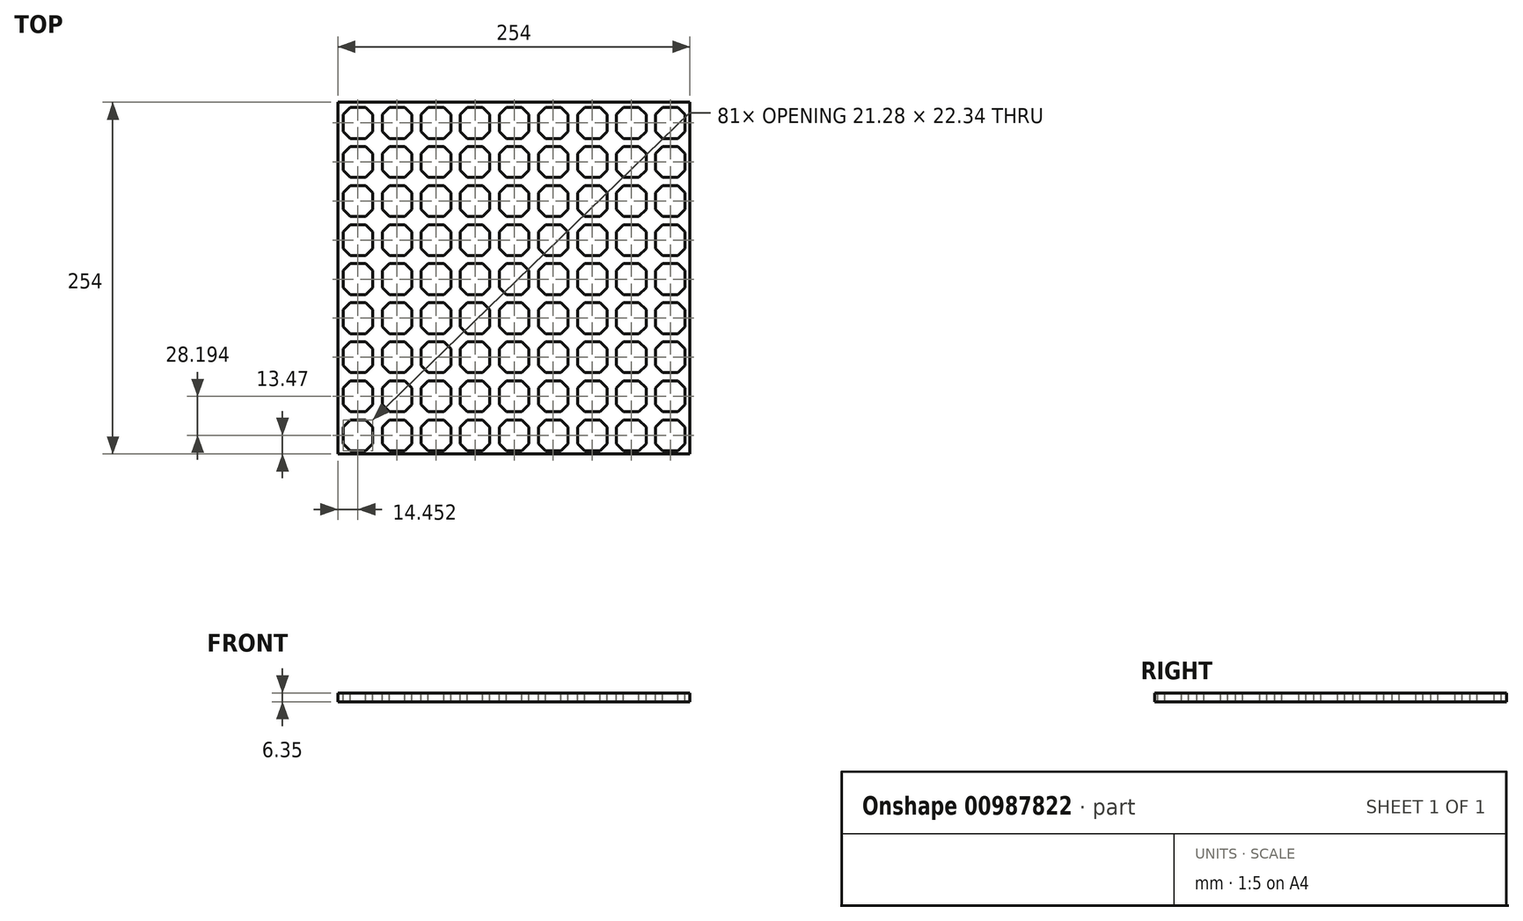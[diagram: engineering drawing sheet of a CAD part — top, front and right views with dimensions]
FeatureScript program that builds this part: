
annotation { "Feature Type Name" : "Feature", "Feature Type Description" : "" }
export const myFeature = defineFeature(function(context is Context, id is Id, definition is map)
    precondition{}
    {
        {
            var Q0;
            Q0=qCreatedBy(makeId("Top.planeOp"),FACE);
            var sketch = newSketch(context, id + "F0", { "sketchPlane" : qUnion([Q0])});
            skLineSegment(sketch, "E0.bottom", {"start": v(-127, 127) * mm, "end": v(127, 127) * mm});
            skLineSegment(sketch, "E0.top", {"start": v(-127, -127) * mm, "end": v(127, -127) * mm});
            skLineSegment(sketch, "E0.left", {"start": v(-127, 127) * mm, "end": v(-127, -127) * mm});
            skLineSegment(sketch, "E0.right", {"start": v(127, 127) * mm, "end": v(127, -127) * mm});
            skSolve(sketch);
        }
        {
            var Q0;
            Q0=qSketchRegion(id+"F0",true);
            extrude(context, id + "F1", {"entities" : qUnion([Q0]), "depth" : 6.35 * mm, "offsetDistance" : 25.4 * mm});
        }
        {
            var Q0;
            Q0=makeQuery(id+"F1.opExtrude","CAP_FACE",FACE,{"disambiguationData":[OSD([sQuery(id+"F0.wireOp",EDGE,"E0.bottom"),sQuery(id+"F0.wireOp",EDGE,"E0.top"),sQuery(id+"F0.wireOp",EDGE,"E0.left"),sQuery(id+"F0.wireOp",EDGE,"E0.right")])],"isStart":false});
            var sketch = newSketch(context, id + "F2", { "sketchPlane" : qUnion([Q0])});
            skLineSegment(sketch, "E1.bottom", {"start": v(-118.11, 123.2) * mm, "end": v(-106.99, 123.2) * mm});
            skLineSegment(sketch, "E1.top", {"start": v(-118.11, 100.85) * mm, "end": v(-106.99, 100.85) * mm});
            skLineSegment(sketch, "E1.left", {"start": v(-123.2, 118.11) * mm, "end": v(-123.2, 105.93) * mm});
            skLineSegment(sketch, "E1.right", {"start": v(-101.9, 118.11) * mm, "end": v(-101.9, 105.93) * mm});
            skLineSegment(sketch, "E2", {"start": v(-123.2, 118.11) * mm, "end": v(-118.11, 123.2) * mm});
            skPoint(sketch, "E3.orphan", {"position": v(-123.2, 123.2) * mm});
            skLineSegment(sketch, "E4", {"start": v(-106.99, 123.2) * mm, "end": v(-101.9, 118.11) * mm});
            skLineSegment(sketch, "E5", {"start": v(-123.2, 105.93) * mm, "end": v(-118.11, 100.85) * mm});
            skLineSegment(sketch, "E6", {"start": v(-101.9, 105.93) * mm, "end": v(-106.99, 100.85) * mm});
            skPoint(sketch, "E7.orphan", {"position": v(-101.9, 123.2) * mm});
            skPoint(sketch, "E8.orphan", {"position": v(-101.9, 100.85) * mm});
            skPoint(sketch, "E9.orphan", {"position": v(-123.2, 100.85) * mm});
            skLineSegment(sketch, "E10.1.0.0", {"start": v(-73.71, 118.11) * mm, "end": v(-73.71, 105.93) * mm});
            skLineSegment(sketch, "E10.1.0.1", {"start": v(-95, 118.11) * mm, "end": v(-95, 105.93) * mm});
            skLineSegment(sketch, "E10.1.0.2", {"start": v(-89.92, 100.85) * mm, "end": v(-78.8, 100.85) * mm});
            skLineSegment(sketch, "E10.1.0.3", {"start": v(-89.92, 123.2) * mm, "end": v(-78.8, 123.2) * mm});
            skPoint(sketch, "E10.1.0.4", {"position": v(-95, 123.2) * mm});
            skPoint(sketch, "E10.1.0.5", {"position": v(-73.71, 100.85) * mm});
            skPoint(sketch, "E10.1.0.6", {"position": v(-73.71, 123.2) * mm});
            skPoint(sketch, "E10.1.0.7", {"position": v(-95, 100.85) * mm});
            skLineSegment(sketch, "E10.1.0.8", {"start": v(-95, 118.11) * mm, "end": v(-89.92, 123.2) * mm});
            skLineSegment(sketch, "E10.1.0.9", {"start": v(-95, 105.93) * mm, "end": v(-89.92, 100.85) * mm});
            skLineSegment(sketch, "E10.1.0.10", {"start": v(-78.8, 123.2) * mm, "end": v(-73.71, 118.11) * mm});
            skLineSegment(sketch, "E10.1.0.11", {"start": v(-73.71, 105.93) * mm, "end": v(-78.8, 100.85) * mm});
            skLineSegment(sketch, "E10.2.0.0", {"start": v(-45.52, 118.11) * mm, "end": v(-45.52, 105.93) * mm});
            skLineSegment(sketch, "E10.2.0.1", {"start": v(-66.8, 118.11) * mm, "end": v(-66.8, 105.93) * mm});
            skLineSegment(sketch, "E10.2.0.2", {"start": v(-61.72, 100.85) * mm, "end": v(-50.6, 100.85) * mm});
            skLineSegment(sketch, "E10.2.0.3", {"start": v(-61.72, 123.2) * mm, "end": v(-50.6, 123.2) * mm});
            skPoint(sketch, "E10.2.0.4", {"position": v(-66.8, 123.2) * mm});
            skPoint(sketch, "E10.2.0.5", {"position": v(-45.52, 100.85) * mm});
            skPoint(sketch, "E10.2.0.6", {"position": v(-45.52, 123.2) * mm});
            skPoint(sketch, "E10.2.0.7", {"position": v(-66.8, 100.85) * mm});
            skLineSegment(sketch, "E10.2.0.8", {"start": v(-66.8, 118.11) * mm, "end": v(-61.72, 123.2) * mm});
            skLineSegment(sketch, "E10.2.0.9", {"start": v(-66.8, 105.93) * mm, "end": v(-61.72, 100.85) * mm});
            skLineSegment(sketch, "E10.2.0.10", {"start": v(-50.6, 123.2) * mm, "end": v(-45.52, 118.11) * mm});
            skLineSegment(sketch, "E10.2.0.11", {"start": v(-45.52, 105.93) * mm, "end": v(-50.6, 100.85) * mm});
            skLineSegment(sketch, "E10.3.0.0", {"start": v(-17.32, 118.11) * mm, "end": v(-17.32, 105.93) * mm});
            skLineSegment(sketch, "E10.3.0.1", {"start": v(-38.6, 118.11) * mm, "end": v(-38.6, 105.93) * mm});
            skLineSegment(sketch, "E10.3.0.2", {"start": v(-33.53, 100.85) * mm, "end": v(-22.4, 100.85) * mm});
            skLineSegment(sketch, "E10.3.0.3", {"start": v(-33.53, 123.2) * mm, "end": v(-22.4, 123.2) * mm});
            skPoint(sketch, "E10.3.0.4", {"position": v(-38.6, 123.2) * mm});
            skPoint(sketch, "E10.3.0.5", {"position": v(-17.32, 100.85) * mm});
            skPoint(sketch, "E10.3.0.6", {"position": v(-17.32, 123.2) * mm});
            skPoint(sketch, "E10.3.0.7", {"position": v(-38.6, 100.85) * mm});
            skLineSegment(sketch, "E10.3.0.8", {"start": v(-38.6, 118.11) * mm, "end": v(-33.53, 123.2) * mm});
            skLineSegment(sketch, "E10.3.0.9", {"start": v(-38.6, 105.93) * mm, "end": v(-33.53, 100.85) * mm});
            skLineSegment(sketch, "E10.3.0.10", {"start": v(-22.4, 123.2) * mm, "end": v(-17.32, 118.11) * mm});
            skLineSegment(sketch, "E10.3.0.11", {"start": v(-17.32, 105.93) * mm, "end": v(-22.4, 100.85) * mm});
            skLineSegment(sketch, "E10.4.0.0", {"start": v(10.87, 118.11) * mm, "end": v(10.87, 105.93) * mm});
            skLineSegment(sketch, "E10.4.0.1", {"start": v(-10.41, 118.11) * mm, "end": v(-10.41, 105.93) * mm});
            skLineSegment(sketch, "E10.4.0.2", {"start": v(-5.33, 100.85) * mm, "end": v(5.79, 100.85) * mm});
            skLineSegment(sketch, "E10.4.0.3", {"start": v(-5.33, 123.2) * mm, "end": v(5.79, 123.2) * mm});
            skPoint(sketch, "E10.4.0.4", {"position": v(-10.41, 123.2) * mm});
            skPoint(sketch, "E10.4.0.5", {"position": v(10.87, 100.85) * mm});
            skPoint(sketch, "E10.4.0.6", {"position": v(10.87, 123.2) * mm});
            skPoint(sketch, "E10.4.0.7", {"position": v(-10.41, 100.85) * mm});
            skLineSegment(sketch, "E10.4.0.8", {"start": v(-10.41, 118.11) * mm, "end": v(-5.33, 123.2) * mm});
            skLineSegment(sketch, "E10.4.0.9", {"start": v(-10.41, 105.93) * mm, "end": v(-5.33, 100.85) * mm});
            skLineSegment(sketch, "E10.4.0.10", {"start": v(5.79, 123.2) * mm, "end": v(10.87, 118.11) * mm});
            skLineSegment(sketch, "E10.4.0.11", {"start": v(10.87, 105.93) * mm, "end": v(5.79, 100.85) * mm});
            skLineSegment(sketch, "E10.5.0.0", {"start": v(39.06, 118.11) * mm, "end": v(39.06, 105.93) * mm});
            skLineSegment(sketch, "E10.5.0.1", {"start": v(17.78, 118.11) * mm, "end": v(17.78, 105.93) * mm});
            skLineSegment(sketch, "E10.5.0.2", {"start": v(22.86, 100.85) * mm, "end": v(33.98, 100.85) * mm});
            skLineSegment(sketch, "E10.5.0.3", {"start": v(22.86, 123.2) * mm, "end": v(33.98, 123.2) * mm});
            skPoint(sketch, "E10.5.0.4", {"position": v(17.78, 123.2) * mm});
            skPoint(sketch, "E10.5.0.5", {"position": v(39.06, 100.85) * mm});
            skPoint(sketch, "E10.5.0.6", {"position": v(39.06, 123.2) * mm});
            skPoint(sketch, "E10.5.0.7", {"position": v(17.78, 100.85) * mm});
            skLineSegment(sketch, "E10.5.0.8", {"start": v(17.78, 118.11) * mm, "end": v(22.86, 123.2) * mm});
            skLineSegment(sketch, "E10.5.0.9", {"start": v(17.78, 105.93) * mm, "end": v(22.86, 100.85) * mm});
            skLineSegment(sketch, "E10.5.0.10", {"start": v(33.98, 123.2) * mm, "end": v(39.06, 118.11) * mm});
            skLineSegment(sketch, "E10.5.0.11", {"start": v(39.06, 105.93) * mm, "end": v(33.98, 100.85) * mm});
            skLineSegment(sketch, "E10.6.0.0", {"start": v(67.26, 118.11) * mm, "end": v(67.26, 105.93) * mm});
            skLineSegment(sketch, "E10.6.0.1", {"start": v(45.97, 118.11) * mm, "end": v(45.97, 105.93) * mm});
            skLineSegment(sketch, "E10.6.0.2", {"start": v(51.05, 100.85) * mm, "end": v(62.18, 100.85) * mm});
            skLineSegment(sketch, "E10.6.0.3", {"start": v(51.05, 123.2) * mm, "end": v(62.18, 123.2) * mm});
            skPoint(sketch, "E10.6.0.4", {"position": v(45.97, 123.2) * mm});
            skPoint(sketch, "E10.6.0.5", {"position": v(67.26, 100.85) * mm});
            skPoint(sketch, "E10.6.0.6", {"position": v(67.26, 123.2) * mm});
            skPoint(sketch, "E10.6.0.7", {"position": v(45.97, 100.85) * mm});
            skLineSegment(sketch, "E10.6.0.8", {"start": v(45.97, 118.11) * mm, "end": v(51.05, 123.2) * mm});
            skLineSegment(sketch, "E10.6.0.9", {"start": v(45.97, 105.93) * mm, "end": v(51.05, 100.85) * mm});
            skLineSegment(sketch, "E10.6.0.10", {"start": v(62.18, 123.2) * mm, "end": v(67.26, 118.11) * mm});
            skLineSegment(sketch, "E10.6.0.11", {"start": v(67.26, 105.93) * mm, "end": v(62.18, 100.85) * mm});
            skLineSegment(sketch, "E10.7.0.0", {"start": v(95.45, 118.11) * mm, "end": v(95.45, 105.93) * mm});
            skLineSegment(sketch, "E10.7.0.1", {"start": v(74.17, 118.11) * mm, "end": v(74.17, 105.93) * mm});
            skLineSegment(sketch, "E10.7.0.2", {"start": v(79.25, 100.85) * mm, "end": v(90.37, 100.85) * mm});
            skLineSegment(sketch, "E10.7.0.3", {"start": v(79.25, 123.2) * mm, "end": v(90.37, 123.2) * mm});
            skPoint(sketch, "E10.7.0.4", {"position": v(74.17, 123.2) * mm});
            skPoint(sketch, "E10.7.0.5", {"position": v(95.45, 100.85) * mm});
            skPoint(sketch, "E10.7.0.6", {"position": v(95.45, 123.2) * mm});
            skPoint(sketch, "E10.7.0.7", {"position": v(74.17, 100.85) * mm});
            skLineSegment(sketch, "E10.7.0.8", {"start": v(74.17, 118.11) * mm, "end": v(79.25, 123.2) * mm});
            skLineSegment(sketch, "E10.7.0.9", {"start": v(74.17, 105.93) * mm, "end": v(79.25, 100.85) * mm});
            skLineSegment(sketch, "E10.7.0.10", {"start": v(90.37, 123.2) * mm, "end": v(95.45, 118.11) * mm});
            skLineSegment(sketch, "E10.7.0.11", {"start": v(95.45, 105.93) * mm, "end": v(90.37, 100.85) * mm});
            skLineSegment(sketch, "E10.8.0.0", {"start": v(123.65, 118.11) * mm, "end": v(123.65, 105.93) * mm});
            skLineSegment(sketch, "E10.8.0.1", {"start": v(102.36, 118.11) * mm, "end": v(102.36, 105.93) * mm});
            skLineSegment(sketch, "E10.8.0.2", {"start": v(107.44, 100.85) * mm, "end": v(118.57, 100.85) * mm});
            skLineSegment(sketch, "E10.8.0.3", {"start": v(107.44, 123.2) * mm, "end": v(118.57, 123.2) * mm});
            skPoint(sketch, "E10.8.0.4", {"position": v(102.36, 123.2) * mm});
            skPoint(sketch, "E10.8.0.5", {"position": v(123.65, 100.85) * mm});
            skPoint(sketch, "E10.8.0.6", {"position": v(123.65, 123.2) * mm});
            skPoint(sketch, "E10.8.0.7", {"position": v(102.36, 100.85) * mm});
            skLineSegment(sketch, "E10.8.0.8", {"start": v(102.36, 118.11) * mm, "end": v(107.44, 123.2) * mm});
            skLineSegment(sketch, "E10.8.0.9", {"start": v(102.36, 105.93) * mm, "end": v(107.44, 100.85) * mm});
            skLineSegment(sketch, "E10.8.0.10", {"start": v(118.57, 123.2) * mm, "end": v(123.65, 118.11) * mm});
            skLineSegment(sketch, "E10.8.0.11", {"start": v(123.65, 105.93) * mm, "end": v(118.57, 100.85) * mm});
            skLineSegment(sketch, "E10.9.0.0", {"start": v(151.84, 118.11) * mm, "end": v(151.84, 105.93) * mm});
            skLineSegment(sketch, "E10.9.0.1", {"start": v(130.56, 118.11) * mm, "end": v(130.56, 105.93) * mm});
            skLineSegment(sketch, "E10.9.0.2", {"start": v(135.64, 100.85) * mm, "end": v(146.76, 100.85) * mm});
            skLineSegment(sketch, "E10.9.0.3", {"start": v(135.64, 123.2) * mm, "end": v(146.76, 123.2) * mm});
            skPoint(sketch, "E10.9.0.4", {"position": v(130.56, 123.2) * mm});
            skPoint(sketch, "E10.9.0.5", {"position": v(151.84, 100.85) * mm});
            skPoint(sketch, "E10.9.0.6", {"position": v(151.84, 123.2) * mm});
            skPoint(sketch, "E10.9.0.7", {"position": v(130.56, 100.85) * mm});
            skLineSegment(sketch, "E10.9.0.8", {"start": v(130.56, 118.11) * mm, "end": v(135.64, 123.2) * mm});
            skLineSegment(sketch, "E10.9.0.9", {"start": v(130.56, 105.93) * mm, "end": v(135.64, 100.85) * mm});
            skLineSegment(sketch, "E10.9.0.10", {"start": v(146.76, 123.2) * mm, "end": v(151.84, 118.11) * mm});
            skLineSegment(sketch, "E10.9.0.11", {"start": v(151.84, 105.93) * mm, "end": v(146.76, 100.85) * mm});
            skLineSegment(sketch, "E10.direction1", {"start": v(-123.2, 100.85) * mm, "end": v(-95, 100.85) * mm, "construction": true});
            skPoint(sketch, "E11.0.1.0", {"position": v(-73.71, 95) * mm});
            skLineSegment(sketch, "E11.0.1.1", {"start": v(102.36, 89.92) * mm, "end": v(102.36, 77.74) * mm});
            skLineSegment(sketch, "E11.0.1.2", {"start": v(45.97, 89.92) * mm, "end": v(45.97, 77.74) * mm});
            skPoint(sketch, "E11.0.1.3", {"position": v(39.06, 95) * mm});
            skLineSegment(sketch, "E11.0.1.4", {"start": v(-66.8, 89.92) * mm, "end": v(-66.8, 77.74) * mm});
            skLineSegment(sketch, "E11.0.1.5", {"start": v(-95, 89.92) * mm, "end": v(-95, 77.74) * mm});
            skLineSegment(sketch, "E11.0.1.6", {"start": v(-73.71, 89.92) * mm, "end": v(-73.71, 77.74) * mm});
            skLineSegment(sketch, "E11.0.1.7", {"start": v(-123.2, 89.92) * mm, "end": v(-123.2, 77.74) * mm});
            skLineSegment(sketch, "E11.0.1.8", {"start": v(-101.9, 89.92) * mm, "end": v(-101.9, 77.74) * mm});
            skPoint(sketch, "E11.0.1.9", {"position": v(130.56, 72.66) * mm});
            skPoint(sketch, "E11.0.1.10", {"position": v(67.26, 95) * mm});
            skPoint(sketch, "E11.0.1.11", {"position": v(-66.8, 72.66) * mm});
            skPoint(sketch, "E11.0.1.12", {"position": v(10.87, 95) * mm});
            skPoint(sketch, "E11.0.1.13", {"position": v(-101.9, 72.66) * mm});
            skPoint(sketch, "E11.0.1.14", {"position": v(45.97, 72.66) * mm});
            skLineSegment(sketch, "E11.0.1.15", {"start": v(-118.11, 95) * mm, "end": v(-106.99, 95) * mm});
            skPoint(sketch, "E11.0.1.16", {"position": v(-45.52, 95) * mm});
            skPoint(sketch, "E11.0.1.17", {"position": v(151.84, 95) * mm});
            skPoint(sketch, "E11.0.1.18", {"position": v(123.65, 95) * mm});
            skLineSegment(sketch, "E11.0.1.19", {"start": v(151.84, 89.92) * mm, "end": v(151.84, 77.74) * mm});
            skLineSegment(sketch, "E11.0.1.20", {"start": v(95.45, 89.92) * mm, "end": v(95.45, 77.74) * mm});
            skLineSegment(sketch, "E11.0.1.21", {"start": v(39.06, 89.92) * mm, "end": v(39.06, 77.74) * mm});
            skLineSegment(sketch, "E11.0.1.22", {"start": v(-17.32, 89.92) * mm, "end": v(-17.32, 77.74) * mm});
            skPoint(sketch, "E11.0.1.23", {"position": v(74.17, 72.66) * mm});
            skPoint(sketch, "E11.0.1.24", {"position": v(-38.6, 72.66) * mm});
            skLineSegment(sketch, "E11.0.1.25", {"start": v(-10.41, 89.92) * mm, "end": v(-10.41, 77.74) * mm});
            skLineSegment(sketch, "E11.0.1.26", {"start": v(-89.92, 72.66) * mm, "end": v(-78.8, 72.66) * mm});
            skLineSegment(sketch, "E11.0.1.27", {"start": v(-45.52, 89.92) * mm, "end": v(-45.52, 77.74) * mm});
            skLineSegment(sketch, "E11.0.1.28", {"start": v(10.87, 89.92) * mm, "end": v(10.87, 77.74) * mm});
            skPoint(sketch, "E11.0.1.29", {"position": v(-17.32, 95) * mm});
            skPoint(sketch, "E11.0.1.30", {"position": v(95.45, 95) * mm});
            skPoint(sketch, "E11.0.1.31", {"position": v(95.45, 72.66) * mm});
            skPoint(sketch, "E11.0.1.32", {"position": v(151.84, 72.66) * mm});
            skPoint(sketch, "E11.0.1.33", {"position": v(-73.71, 72.66) * mm});
            skPoint(sketch, "E11.0.1.34", {"position": v(39.06, 72.66) * mm});
            skLineSegment(sketch, "E11.0.1.35", {"start": v(67.26, 89.92) * mm, "end": v(67.26, 77.74) * mm});
            skLineSegment(sketch, "E11.0.1.36", {"start": v(123.65, 89.92) * mm, "end": v(123.65, 77.74) * mm});
            skLineSegment(sketch, "E11.0.1.37", {"start": v(-123.2, 72.66) * mm, "end": v(-95, 72.66) * mm, "construction": true});
            skPoint(sketch, "E11.0.1.38", {"position": v(130.56, 95) * mm});
            skPoint(sketch, "E11.0.1.39", {"position": v(45.97, 95) * mm});
            skLineSegment(sketch, "E11.0.1.40", {"start": v(51.05, 95) * mm, "end": v(62.18, 95) * mm});
            skPoint(sketch, "E11.0.1.41", {"position": v(-66.8, 95) * mm});
            skLineSegment(sketch, "E11.0.1.42", {"start": v(107.44, 95) * mm, "end": v(118.57, 95) * mm});
            skLineSegment(sketch, "E11.0.1.43", {"start": v(135.64, 95) * mm, "end": v(146.76, 95) * mm});
            skLineSegment(sketch, "E11.0.1.44", {"start": v(79.25, 95) * mm, "end": v(90.37, 95) * mm});
            skLineSegment(sketch, "E11.0.1.45", {"start": v(22.86, 95) * mm, "end": v(33.98, 95) * mm});
            skLineSegment(sketch, "E11.0.1.46", {"start": v(-33.53, 95) * mm, "end": v(-22.4, 95) * mm});
            skLineSegment(sketch, "E11.0.1.47", {"start": v(-61.72, 95) * mm, "end": v(-50.6, 95) * mm});
            skPoint(sketch, "E11.0.1.48", {"position": v(-17.32, 72.66) * mm});
            skLineSegment(sketch, "E11.0.1.49", {"start": v(-5.33, 95) * mm, "end": v(5.79, 95) * mm});
            skLineSegment(sketch, "E11.0.1.50", {"start": v(-33.53, 72.66) * mm, "end": v(-22.4, 72.66) * mm});
            skLineSegment(sketch, "E11.0.1.51", {"start": v(22.86, 72.66) * mm, "end": v(33.98, 72.66) * mm});
            skPoint(sketch, "E11.0.1.52", {"position": v(17.78, 95) * mm});
            skLineSegment(sketch, "E11.0.1.53", {"start": v(79.25, 72.66) * mm, "end": v(90.37, 72.66) * mm});
            skLineSegment(sketch, "E11.0.1.54", {"start": v(135.64, 72.66) * mm, "end": v(146.76, 72.66) * mm});
            skPoint(sketch, "E11.0.1.55", {"position": v(67.26, 72.66) * mm});
            skPoint(sketch, "E11.0.1.56", {"position": v(-101.9, 95) * mm});
            skPoint(sketch, "E11.0.1.57", {"position": v(10.87, 72.66) * mm});
            skPoint(sketch, "E11.0.1.58", {"position": v(123.65, 72.66) * mm});
            skPoint(sketch, "E11.0.1.59", {"position": v(-45.52, 72.66) * mm});
            skPoint(sketch, "E11.0.1.60", {"position": v(-95, 72.66) * mm});
            skLineSegment(sketch, "E11.0.1.61", {"start": v(51.05, 72.66) * mm, "end": v(62.18, 72.66) * mm});
            skPoint(sketch, "E11.0.1.62", {"position": v(17.78, 72.66) * mm});
            skLineSegment(sketch, "E11.0.1.63", {"start": v(107.44, 72.66) * mm, "end": v(118.57, 72.66) * mm});
            skLineSegment(sketch, "E11.0.1.64", {"start": v(-61.72, 72.66) * mm, "end": v(-50.6, 72.66) * mm});
            skLineSegment(sketch, "E11.0.1.65", {"start": v(-5.33, 72.66) * mm, "end": v(5.79, 72.66) * mm});
            skPoint(sketch, "E11.0.1.66", {"position": v(-123.2, 95) * mm});
            skPoint(sketch, "E11.0.1.67", {"position": v(-10.41, 95) * mm});
            skPoint(sketch, "E11.0.1.68", {"position": v(102.36, 95) * mm});
            skPoint(sketch, "E11.0.1.69", {"position": v(74.17, 95) * mm});
            skPoint(sketch, "E11.0.1.70", {"position": v(-10.41, 72.66) * mm});
            skPoint(sketch, "E11.0.1.71", {"position": v(102.36, 72.66) * mm});
            skPoint(sketch, "E11.0.1.72", {"position": v(-38.6, 95) * mm});
            skPoint(sketch, "E11.0.1.73", {"position": v(-123.2, 72.66) * mm});
            skPoint(sketch, "E11.0.1.74", {"position": v(-95, 95) * mm});
            skLineSegment(sketch, "E11.0.1.75", {"start": v(-38.6, 89.92) * mm, "end": v(-38.6, 77.74) * mm});
            skLineSegment(sketch, "E11.0.1.76", {"start": v(17.78, 89.92) * mm, "end": v(17.78, 77.74) * mm});
            skLineSegment(sketch, "E11.0.1.77", {"start": v(74.17, 89.92) * mm, "end": v(74.17, 77.74) * mm});
            skLineSegment(sketch, "E11.0.1.78", {"start": v(130.56, 89.92) * mm, "end": v(130.56, 77.74) * mm});
            skLineSegment(sketch, "E11.0.1.79", {"start": v(-118.11, 72.66) * mm, "end": v(-106.99, 72.66) * mm});
            skLineSegment(sketch, "E11.0.1.80", {"start": v(-89.92, 95) * mm, "end": v(-78.8, 95) * mm});
            skLineSegment(sketch, "E11.0.1.81", {"start": v(-78.8, 95) * mm, "end": v(-73.71, 89.92) * mm});
            skLineSegment(sketch, "E11.0.1.82", {"start": v(-95, 77.74) * mm, "end": v(-89.92, 72.66) * mm});
            skLineSegment(sketch, "E11.0.1.83", {"start": v(33.98, 95) * mm, "end": v(39.06, 89.92) * mm});
            skLineSegment(sketch, "E11.0.1.84", {"start": v(-73.71, 77.74) * mm, "end": v(-78.8, 72.66) * mm});
            skLineSegment(sketch, "E11.0.1.85", {"start": v(-123.2, 89.92) * mm, "end": v(-118.11, 95) * mm});
            skLineSegment(sketch, "E11.0.1.86", {"start": v(-106.99, 95) * mm, "end": v(-101.9, 89.92) * mm});
            skLineSegment(sketch, "E11.0.1.87", {"start": v(-123.2, 77.74) * mm, "end": v(-118.11, 72.66) * mm});
            skLineSegment(sketch, "E11.0.1.88", {"start": v(-101.9, 77.74) * mm, "end": v(-106.99, 72.66) * mm});
            skLineSegment(sketch, "E11.0.1.89", {"start": v(-45.52, 77.74) * mm, "end": v(-50.6, 72.66) * mm});
            skLineSegment(sketch, "E11.0.1.90", {"start": v(10.87, 77.74) * mm, "end": v(5.79, 72.66) * mm});
            skLineSegment(sketch, "E11.0.1.91", {"start": v(67.26, 77.74) * mm, "end": v(62.18, 72.66) * mm});
            skLineSegment(sketch, "E11.0.1.92", {"start": v(123.65, 77.74) * mm, "end": v(118.57, 72.66) * mm});
            skLineSegment(sketch, "E11.0.1.93", {"start": v(62.18, 95) * mm, "end": v(67.26, 89.92) * mm});
            skLineSegment(sketch, "E11.0.1.94", {"start": v(39.06, 77.74) * mm, "end": v(33.98, 72.66) * mm});
            skLineSegment(sketch, "E11.0.1.95", {"start": v(118.57, 95) * mm, "end": v(123.65, 89.92) * mm});
            skLineSegment(sketch, "E11.0.1.96", {"start": v(95.45, 77.74) * mm, "end": v(90.37, 72.66) * mm});
            skLineSegment(sketch, "E11.0.1.97", {"start": v(151.84, 77.74) * mm, "end": v(146.76, 72.66) * mm});
            skLineSegment(sketch, "E11.0.1.98", {"start": v(-50.6, 95) * mm, "end": v(-45.52, 89.92) * mm});
            skLineSegment(sketch, "E11.0.1.99", {"start": v(5.79, 95) * mm, "end": v(10.87, 89.92) * mm});
            skLineSegment(sketch, "E11.0.1.100", {"start": v(-17.32, 77.74) * mm, "end": v(-22.4, 72.66) * mm});
            skLineSegment(sketch, "E11.0.1.101", {"start": v(-38.6, 77.74) * mm, "end": v(-33.53, 72.66) * mm});
            skLineSegment(sketch, "E11.0.1.102", {"start": v(-10.41, 89.92) * mm, "end": v(-5.33, 95) * mm});
            skLineSegment(sketch, "E11.0.1.103", {"start": v(-66.8, 89.92) * mm, "end": v(-61.72, 95) * mm});
            skLineSegment(sketch, "E11.0.1.104", {"start": v(130.56, 77.74) * mm, "end": v(135.64, 72.66) * mm});
            skLineSegment(sketch, "E11.0.1.105", {"start": v(102.36, 89.92) * mm, "end": v(107.44, 95) * mm});
            skLineSegment(sketch, "E11.0.1.106", {"start": v(74.17, 77.74) * mm, "end": v(79.25, 72.66) * mm});
            skLineSegment(sketch, "E11.0.1.107", {"start": v(45.97, 89.92) * mm, "end": v(51.05, 95) * mm});
            skLineSegment(sketch, "E11.0.1.108", {"start": v(17.78, 77.74) * mm, "end": v(22.86, 72.66) * mm});
            skLineSegment(sketch, "E11.0.1.109", {"start": v(130.56, 89.92) * mm, "end": v(135.64, 95) * mm});
            skLineSegment(sketch, "E11.0.1.110", {"start": v(74.17, 89.92) * mm, "end": v(79.25, 95) * mm});
            skLineSegment(sketch, "E11.0.1.111", {"start": v(17.78, 89.92) * mm, "end": v(22.86, 95) * mm});
            skLineSegment(sketch, "E11.0.1.112", {"start": v(-95, 89.92) * mm, "end": v(-89.92, 95) * mm});
            skLineSegment(sketch, "E11.0.1.113", {"start": v(-38.6, 89.92) * mm, "end": v(-33.53, 95) * mm});
            skLineSegment(sketch, "E11.0.1.114", {"start": v(-22.4, 95) * mm, "end": v(-17.32, 89.92) * mm});
            skLineSegment(sketch, "E11.0.1.115", {"start": v(-10.41, 77.74) * mm, "end": v(-5.33, 72.66) * mm});
            skLineSegment(sketch, "E11.0.1.116", {"start": v(-66.8, 77.74) * mm, "end": v(-61.72, 72.66) * mm});
            skLineSegment(sketch, "E11.0.1.117", {"start": v(146.76, 95) * mm, "end": v(151.84, 89.92) * mm});
            skLineSegment(sketch, "E11.0.1.118", {"start": v(102.36, 77.74) * mm, "end": v(107.44, 72.66) * mm});
            skLineSegment(sketch, "E11.0.1.119", {"start": v(90.37, 95) * mm, "end": v(95.45, 89.92) * mm});
            skLineSegment(sketch, "E11.0.1.120", {"start": v(45.97, 77.74) * mm, "end": v(51.05, 72.66) * mm});
            skPoint(sketch, "E11.0.2.0", {"position": v(-73.71, 66.8) * mm});
            skLineSegment(sketch, "E11.0.2.1", {"start": v(102.36, 61.72) * mm, "end": v(102.36, 49.55) * mm});
            skLineSegment(sketch, "E11.0.2.2", {"start": v(45.97, 61.72) * mm, "end": v(45.97, 49.55) * mm});
            skPoint(sketch, "E11.0.2.3", {"position": v(39.06, 66.8) * mm});
            skLineSegment(sketch, "E11.0.2.4", {"start": v(-66.8, 61.72) * mm, "end": v(-66.8, 49.55) * mm});
            skLineSegment(sketch, "E11.0.2.5", {"start": v(-95, 61.72) * mm, "end": v(-95, 49.55) * mm});
            skLineSegment(sketch, "E11.0.2.6", {"start": v(-73.71, 61.72) * mm, "end": v(-73.71, 49.55) * mm});
            skLineSegment(sketch, "E11.0.2.7", {"start": v(-123.2, 61.72) * mm, "end": v(-123.2, 49.55) * mm});
            skLineSegment(sketch, "E11.0.2.8", {"start": v(-101.9, 61.72) * mm, "end": v(-101.9, 49.55) * mm});
            skPoint(sketch, "E11.0.2.9", {"position": v(130.56, 44.47) * mm});
            skPoint(sketch, "E11.0.2.10", {"position": v(67.26, 66.8) * mm});
            skPoint(sketch, "E11.0.2.11", {"position": v(-66.8, 44.47) * mm});
            skPoint(sketch, "E11.0.2.12", {"position": v(10.87, 66.8) * mm});
            skPoint(sketch, "E11.0.2.13", {"position": v(-101.9, 44.47) * mm});
            skPoint(sketch, "E11.0.2.14", {"position": v(45.97, 44.47) * mm});
            skLineSegment(sketch, "E11.0.2.15", {"start": v(-118.11, 66.8) * mm, "end": v(-106.99, 66.8) * mm});
            skPoint(sketch, "E11.0.2.16", {"position": v(-45.52, 66.8) * mm});
            skPoint(sketch, "E11.0.2.17", {"position": v(151.84, 66.8) * mm});
            skPoint(sketch, "E11.0.2.18", {"position": v(123.65, 66.8) * mm});
            skLineSegment(sketch, "E11.0.2.19", {"start": v(151.84, 61.72) * mm, "end": v(151.84, 49.55) * mm});
            skLineSegment(sketch, "E11.0.2.20", {"start": v(95.45, 61.72) * mm, "end": v(95.45, 49.55) * mm});
            skLineSegment(sketch, "E11.0.2.21", {"start": v(39.06, 61.72) * mm, "end": v(39.06, 49.55) * mm});
            skLineSegment(sketch, "E11.0.2.22", {"start": v(-17.32, 61.72) * mm, "end": v(-17.32, 49.55) * mm});
            skPoint(sketch, "E11.0.2.23", {"position": v(74.17, 44.47) * mm});
            skPoint(sketch, "E11.0.2.24", {"position": v(-38.6, 44.47) * mm});
            skLineSegment(sketch, "E11.0.2.25", {"start": v(-10.41, 61.72) * mm, "end": v(-10.41, 49.55) * mm});
            skLineSegment(sketch, "E11.0.2.26", {"start": v(-89.92, 44.47) * mm, "end": v(-78.8, 44.47) * mm});
            skLineSegment(sketch, "E11.0.2.27", {"start": v(-45.52, 61.72) * mm, "end": v(-45.52, 49.55) * mm});
            skLineSegment(sketch, "E11.0.2.28", {"start": v(10.87, 61.72) * mm, "end": v(10.87, 49.55) * mm});
            skPoint(sketch, "E11.0.2.29", {"position": v(-17.32, 66.8) * mm});
            skPoint(sketch, "E11.0.2.30", {"position": v(95.45, 66.8) * mm});
            skPoint(sketch, "E11.0.2.31", {"position": v(95.45, 44.47) * mm});
            skPoint(sketch, "E11.0.2.32", {"position": v(151.84, 44.47) * mm});
            skPoint(sketch, "E11.0.2.33", {"position": v(-73.71, 44.47) * mm});
            skPoint(sketch, "E11.0.2.34", {"position": v(39.06, 44.47) * mm});
            skLineSegment(sketch, "E11.0.2.35", {"start": v(67.26, 61.72) * mm, "end": v(67.26, 49.55) * mm});
            skLineSegment(sketch, "E11.0.2.36", {"start": v(123.65, 61.72) * mm, "end": v(123.65, 49.55) * mm});
            skLineSegment(sketch, "E11.0.2.37", {"start": v(-123.2, 44.47) * mm, "end": v(-95, 44.47) * mm, "construction": true});
            skPoint(sketch, "E11.0.2.38", {"position": v(130.56, 66.8) * mm});
            skPoint(sketch, "E11.0.2.39", {"position": v(45.97, 66.8) * mm});
            skLineSegment(sketch, "E11.0.2.40", {"start": v(51.05, 66.8) * mm, "end": v(62.18, 66.8) * mm});
            skPoint(sketch, "E11.0.2.41", {"position": v(-66.8, 66.8) * mm});
            skLineSegment(sketch, "E11.0.2.42", {"start": v(107.44, 66.8) * mm, "end": v(118.57, 66.8) * mm});
            skLineSegment(sketch, "E11.0.2.43", {"start": v(135.64, 66.8) * mm, "end": v(146.76, 66.8) * mm});
            skLineSegment(sketch, "E11.0.2.44", {"start": v(79.25, 66.8) * mm, "end": v(90.37, 66.8) * mm});
            skLineSegment(sketch, "E11.0.2.45", {"start": v(22.86, 66.8) * mm, "end": v(33.98, 66.8) * mm});
            skLineSegment(sketch, "E11.0.2.46", {"start": v(-33.53, 66.8) * mm, "end": v(-22.4, 66.8) * mm});
            skLineSegment(sketch, "E11.0.2.47", {"start": v(-61.72, 66.8) * mm, "end": v(-50.6, 66.8) * mm});
            skPoint(sketch, "E11.0.2.48", {"position": v(-17.32, 44.47) * mm});
            skLineSegment(sketch, "E11.0.2.49", {"start": v(-5.33, 66.8) * mm, "end": v(5.79, 66.8) * mm});
            skLineSegment(sketch, "E11.0.2.50", {"start": v(-33.53, 44.47) * mm, "end": v(-22.4, 44.47) * mm});
            skLineSegment(sketch, "E11.0.2.51", {"start": v(22.86, 44.47) * mm, "end": v(33.98, 44.47) * mm});
            skPoint(sketch, "E11.0.2.52", {"position": v(17.78, 66.8) * mm});
            skLineSegment(sketch, "E11.0.2.53", {"start": v(79.25, 44.47) * mm, "end": v(90.37, 44.47) * mm});
            skLineSegment(sketch, "E11.0.2.54", {"start": v(135.64, 44.47) * mm, "end": v(146.76, 44.47) * mm});
            skPoint(sketch, "E11.0.2.55", {"position": v(67.26, 44.47) * mm});
            skPoint(sketch, "E11.0.2.56", {"position": v(-101.9, 66.8) * mm});
            skPoint(sketch, "E11.0.2.57", {"position": v(10.87, 44.47) * mm});
            skPoint(sketch, "E11.0.2.58", {"position": v(123.65, 44.47) * mm});
            skPoint(sketch, "E11.0.2.59", {"position": v(-45.52, 44.47) * mm});
            skPoint(sketch, "E11.0.2.60", {"position": v(-95, 44.47) * mm});
            skLineSegment(sketch, "E11.0.2.61", {"start": v(51.05, 44.47) * mm, "end": v(62.18, 44.47) * mm});
            skPoint(sketch, "E11.0.2.62", {"position": v(17.78, 44.47) * mm});
            skLineSegment(sketch, "E11.0.2.63", {"start": v(107.44, 44.47) * mm, "end": v(118.57, 44.47) * mm});
            skLineSegment(sketch, "E11.0.2.64", {"start": v(-61.72, 44.47) * mm, "end": v(-50.6, 44.47) * mm});
            skLineSegment(sketch, "E11.0.2.65", {"start": v(-5.33, 44.47) * mm, "end": v(5.79, 44.47) * mm});
            skPoint(sketch, "E11.0.2.66", {"position": v(-123.2, 66.8) * mm});
            skPoint(sketch, "E11.0.2.67", {"position": v(-10.41, 66.8) * mm});
            skPoint(sketch, "E11.0.2.68", {"position": v(102.36, 66.8) * mm});
            skPoint(sketch, "E11.0.2.69", {"position": v(74.17, 66.8) * mm});
            skPoint(sketch, "E11.0.2.70", {"position": v(-10.41, 44.47) * mm});
            skPoint(sketch, "E11.0.2.71", {"position": v(102.36, 44.47) * mm});
            skPoint(sketch, "E11.0.2.72", {"position": v(-38.6, 66.8) * mm});
            skPoint(sketch, "E11.0.2.73", {"position": v(-123.2, 44.47) * mm});
            skPoint(sketch, "E11.0.2.74", {"position": v(-95, 66.8) * mm});
            skLineSegment(sketch, "E11.0.2.75", {"start": v(-38.6, 61.72) * mm, "end": v(-38.6, 49.55) * mm});
            skLineSegment(sketch, "E11.0.2.76", {"start": v(17.78, 61.72) * mm, "end": v(17.78, 49.55) * mm});
            skLineSegment(sketch, "E11.0.2.77", {"start": v(74.17, 61.72) * mm, "end": v(74.17, 49.55) * mm});
            skLineSegment(sketch, "E11.0.2.78", {"start": v(130.56, 61.72) * mm, "end": v(130.56, 49.55) * mm});
            skLineSegment(sketch, "E11.0.2.79", {"start": v(-118.11, 44.47) * mm, "end": v(-106.99, 44.47) * mm});
            skLineSegment(sketch, "E11.0.2.80", {"start": v(-89.92, 66.8) * mm, "end": v(-78.8, 66.8) * mm});
            skLineSegment(sketch, "E11.0.2.81", {"start": v(-78.8, 66.8) * mm, "end": v(-73.71, 61.72) * mm});
            skLineSegment(sketch, "E11.0.2.82", {"start": v(-95, 49.55) * mm, "end": v(-89.92, 44.47) * mm});
            skLineSegment(sketch, "E11.0.2.83", {"start": v(33.98, 66.8) * mm, "end": v(39.06, 61.72) * mm});
            skLineSegment(sketch, "E11.0.2.84", {"start": v(-73.71, 49.55) * mm, "end": v(-78.8, 44.47) * mm});
            skLineSegment(sketch, "E11.0.2.85", {"start": v(-123.2, 61.72) * mm, "end": v(-118.11, 66.8) * mm});
            skLineSegment(sketch, "E11.0.2.86", {"start": v(-106.99, 66.8) * mm, "end": v(-101.9, 61.72) * mm});
            skLineSegment(sketch, "E11.0.2.87", {"start": v(-123.2, 49.55) * mm, "end": v(-118.11, 44.47) * mm});
            skLineSegment(sketch, "E11.0.2.88", {"start": v(-101.9, 49.55) * mm, "end": v(-106.99, 44.47) * mm});
            skLineSegment(sketch, "E11.0.2.89", {"start": v(-45.52, 49.55) * mm, "end": v(-50.6, 44.47) * mm});
            skLineSegment(sketch, "E11.0.2.90", {"start": v(10.87, 49.55) * mm, "end": v(5.79, 44.47) * mm});
            skLineSegment(sketch, "E11.0.2.91", {"start": v(67.26, 49.55) * mm, "end": v(62.18, 44.47) * mm});
            skLineSegment(sketch, "E11.0.2.92", {"start": v(123.65, 49.55) * mm, "end": v(118.57, 44.47) * mm});
            skLineSegment(sketch, "E11.0.2.93", {"start": v(62.18, 66.8) * mm, "end": v(67.26, 61.72) * mm});
            skLineSegment(sketch, "E11.0.2.94", {"start": v(39.06, 49.55) * mm, "end": v(33.98, 44.47) * mm});
            skLineSegment(sketch, "E11.0.2.95", {"start": v(118.57, 66.8) * mm, "end": v(123.65, 61.72) * mm});
            skLineSegment(sketch, "E11.0.2.96", {"start": v(95.45, 49.55) * mm, "end": v(90.37, 44.47) * mm});
            skLineSegment(sketch, "E11.0.2.97", {"start": v(151.84, 49.55) * mm, "end": v(146.76, 44.47) * mm});
            skLineSegment(sketch, "E11.0.2.98", {"start": v(-50.6, 66.8) * mm, "end": v(-45.52, 61.72) * mm});
            skLineSegment(sketch, "E11.0.2.99", {"start": v(5.79, 66.8) * mm, "end": v(10.87, 61.72) * mm});
            skLineSegment(sketch, "E11.0.2.100", {"start": v(-17.32, 49.55) * mm, "end": v(-22.4, 44.47) * mm});
            skLineSegment(sketch, "E11.0.2.101", {"start": v(-38.6, 49.55) * mm, "end": v(-33.53, 44.47) * mm});
            skLineSegment(sketch, "E11.0.2.102", {"start": v(-10.41, 61.72) * mm, "end": v(-5.33, 66.8) * mm});
            skLineSegment(sketch, "E11.0.2.103", {"start": v(-66.8, 61.72) * mm, "end": v(-61.72, 66.8) * mm});
            skLineSegment(sketch, "E11.0.2.104", {"start": v(130.56, 49.55) * mm, "end": v(135.64, 44.47) * mm});
            skLineSegment(sketch, "E11.0.2.105", {"start": v(102.36, 61.72) * mm, "end": v(107.44, 66.8) * mm});
            skLineSegment(sketch, "E11.0.2.106", {"start": v(74.17, 49.55) * mm, "end": v(79.25, 44.47) * mm});
            skLineSegment(sketch, "E11.0.2.107", {"start": v(45.97, 61.72) * mm, "end": v(51.05, 66.8) * mm});
            skLineSegment(sketch, "E11.0.2.108", {"start": v(17.78, 49.55) * mm, "end": v(22.86, 44.47) * mm});
            skLineSegment(sketch, "E11.0.2.109", {"start": v(130.56, 61.72) * mm, "end": v(135.64, 66.8) * mm});
            skLineSegment(sketch, "E11.0.2.110", {"start": v(74.17, 61.72) * mm, "end": v(79.25, 66.8) * mm});
            skLineSegment(sketch, "E11.0.2.111", {"start": v(17.78, 61.72) * mm, "end": v(22.86, 66.8) * mm});
            skLineSegment(sketch, "E11.0.2.112", {"start": v(-95, 61.72) * mm, "end": v(-89.92, 66.8) * mm});
            skLineSegment(sketch, "E11.0.2.113", {"start": v(-38.6, 61.72) * mm, "end": v(-33.53, 66.8) * mm});
            skLineSegment(sketch, "E11.0.2.114", {"start": v(-22.4, 66.8) * mm, "end": v(-17.32, 61.72) * mm});
            skLineSegment(sketch, "E11.0.2.115", {"start": v(-10.41, 49.55) * mm, "end": v(-5.33, 44.47) * mm});
            skLineSegment(sketch, "E11.0.2.116", {"start": v(-66.8, 49.55) * mm, "end": v(-61.72, 44.47) * mm});
            skLineSegment(sketch, "E11.0.2.117", {"start": v(146.76, 66.8) * mm, "end": v(151.84, 61.72) * mm});
            skLineSegment(sketch, "E11.0.2.118", {"start": v(102.36, 49.55) * mm, "end": v(107.44, 44.47) * mm});
            skLineSegment(sketch, "E11.0.2.119", {"start": v(90.37, 66.8) * mm, "end": v(95.45, 61.72) * mm});
            skLineSegment(sketch, "E11.0.2.120", {"start": v(45.97, 49.55) * mm, "end": v(51.05, 44.47) * mm});
            skPoint(sketch, "E11.0.3.0", {"position": v(-73.71, 38.6) * mm});
            skLineSegment(sketch, "E11.0.3.1", {"start": v(102.36, 33.53) * mm, "end": v(102.36, 21.35) * mm});
            skLineSegment(sketch, "E11.0.3.2", {"start": v(45.97, 33.53) * mm, "end": v(45.97, 21.35) * mm});
            skPoint(sketch, "E11.0.3.3", {"position": v(39.06, 38.6) * mm});
            skLineSegment(sketch, "E11.0.3.4", {"start": v(-66.8, 33.53) * mm, "end": v(-66.8, 21.35) * mm});
            skLineSegment(sketch, "E11.0.3.5", {"start": v(-95, 33.53) * mm, "end": v(-95, 21.35) * mm});
            skLineSegment(sketch, "E11.0.3.6", {"start": v(-73.71, 33.53) * mm, "end": v(-73.71, 21.35) * mm});
            skLineSegment(sketch, "E11.0.3.7", {"start": v(-123.2, 33.53) * mm, "end": v(-123.2, 21.35) * mm});
            skLineSegment(sketch, "E11.0.3.8", {"start": v(-101.9, 33.53) * mm, "end": v(-101.9, 21.35) * mm});
            skPoint(sketch, "E11.0.3.9", {"position": v(130.56, 16.27) * mm});
            skPoint(sketch, "E11.0.3.10", {"position": v(67.26, 38.6) * mm});
            skPoint(sketch, "E11.0.3.11", {"position": v(-66.8, 16.27) * mm});
            skPoint(sketch, "E11.0.3.12", {"position": v(10.87, 38.6) * mm});
            skPoint(sketch, "E11.0.3.13", {"position": v(-101.9, 16.27) * mm});
            skPoint(sketch, "E11.0.3.14", {"position": v(45.97, 16.27) * mm});
            skLineSegment(sketch, "E11.0.3.15", {"start": v(-118.11, 38.6) * mm, "end": v(-106.99, 38.6) * mm});
            skPoint(sketch, "E11.0.3.16", {"position": v(-45.52, 38.6) * mm});
            skPoint(sketch, "E11.0.3.17", {"position": v(151.84, 38.6) * mm});
            skPoint(sketch, "E11.0.3.18", {"position": v(123.65, 38.6) * mm});
            skLineSegment(sketch, "E11.0.3.19", {"start": v(151.84, 33.53) * mm, "end": v(151.84, 21.35) * mm});
            skLineSegment(sketch, "E11.0.3.20", {"start": v(95.45, 33.53) * mm, "end": v(95.45, 21.35) * mm});
            skLineSegment(sketch, "E11.0.3.21", {"start": v(39.06, 33.53) * mm, "end": v(39.06, 21.35) * mm});
            skLineSegment(sketch, "E11.0.3.22", {"start": v(-17.32, 33.53) * mm, "end": v(-17.32, 21.35) * mm});
            skPoint(sketch, "E11.0.3.23", {"position": v(74.17, 16.27) * mm});
            skPoint(sketch, "E11.0.3.24", {"position": v(-38.6, 16.27) * mm});
            skLineSegment(sketch, "E11.0.3.25", {"start": v(-10.41, 33.53) * mm, "end": v(-10.41, 21.35) * mm});
            skLineSegment(sketch, "E11.0.3.26", {"start": v(-89.92, 16.27) * mm, "end": v(-78.8, 16.27) * mm});
            skLineSegment(sketch, "E11.0.3.27", {"start": v(-45.52, 33.53) * mm, "end": v(-45.52, 21.35) * mm});
            skLineSegment(sketch, "E11.0.3.28", {"start": v(10.87, 33.53) * mm, "end": v(10.87, 21.35) * mm});
            skPoint(sketch, "E11.0.3.29", {"position": v(-17.32, 38.6) * mm});
            skPoint(sketch, "E11.0.3.30", {"position": v(95.45, 38.6) * mm});
            skPoint(sketch, "E11.0.3.31", {"position": v(95.45, 16.27) * mm});
            skPoint(sketch, "E11.0.3.32", {"position": v(151.84, 16.27) * mm});
            skPoint(sketch, "E11.0.3.33", {"position": v(-73.71, 16.27) * mm});
            skPoint(sketch, "E11.0.3.34", {"position": v(39.06, 16.27) * mm});
            skLineSegment(sketch, "E11.0.3.35", {"start": v(67.26, 33.53) * mm, "end": v(67.26, 21.35) * mm});
            skLineSegment(sketch, "E11.0.3.36", {"start": v(123.65, 33.53) * mm, "end": v(123.65, 21.35) * mm});
            skLineSegment(sketch, "E11.0.3.37", {"start": v(-123.2, 16.27) * mm, "end": v(-95, 16.27) * mm, "construction": true});
            skPoint(sketch, "E11.0.3.38", {"position": v(130.56, 38.6) * mm});
            skPoint(sketch, "E11.0.3.39", {"position": v(45.97, 38.6) * mm});
            skLineSegment(sketch, "E11.0.3.40", {"start": v(51.05, 38.6) * mm, "end": v(62.18, 38.6) * mm});
            skPoint(sketch, "E11.0.3.41", {"position": v(-66.8, 38.6) * mm});
            skLineSegment(sketch, "E11.0.3.42", {"start": v(107.44, 38.6) * mm, "end": v(118.57, 38.6) * mm});
            skLineSegment(sketch, "E11.0.3.43", {"start": v(135.64, 38.6) * mm, "end": v(146.76, 38.6) * mm});
            skLineSegment(sketch, "E11.0.3.44", {"start": v(79.25, 38.6) * mm, "end": v(90.37, 38.6) * mm});
            skLineSegment(sketch, "E11.0.3.45", {"start": v(22.86, 38.6) * mm, "end": v(33.98, 38.6) * mm});
            skLineSegment(sketch, "E11.0.3.46", {"start": v(-33.53, 38.6) * mm, "end": v(-22.4, 38.6) * mm});
            skLineSegment(sketch, "E11.0.3.47", {"start": v(-61.72, 38.6) * mm, "end": v(-50.6, 38.6) * mm});
            skPoint(sketch, "E11.0.3.48", {"position": v(-17.32, 16.27) * mm});
            skLineSegment(sketch, "E11.0.3.49", {"start": v(-5.33, 38.6) * mm, "end": v(5.79, 38.6) * mm});
            skLineSegment(sketch, "E11.0.3.50", {"start": v(-33.53, 16.27) * mm, "end": v(-22.4, 16.27) * mm});
            skLineSegment(sketch, "E11.0.3.51", {"start": v(22.86, 16.27) * mm, "end": v(33.98, 16.27) * mm});
            skPoint(sketch, "E11.0.3.52", {"position": v(17.78, 38.6) * mm});
            skLineSegment(sketch, "E11.0.3.53", {"start": v(79.25, 16.27) * mm, "end": v(90.37, 16.27) * mm});
            skLineSegment(sketch, "E11.0.3.54", {"start": v(135.64, 16.27) * mm, "end": v(146.76, 16.27) * mm});
            skPoint(sketch, "E11.0.3.55", {"position": v(67.26, 16.27) * mm});
            skPoint(sketch, "E11.0.3.56", {"position": v(-101.9, 38.6) * mm});
            skPoint(sketch, "E11.0.3.57", {"position": v(10.87, 16.27) * mm});
            skPoint(sketch, "E11.0.3.58", {"position": v(123.65, 16.27) * mm});
            skPoint(sketch, "E11.0.3.59", {"position": v(-45.52, 16.27) * mm});
            skPoint(sketch, "E11.0.3.60", {"position": v(-95, 16.27) * mm});
            skLineSegment(sketch, "E11.0.3.61", {"start": v(51.05, 16.27) * mm, "end": v(62.18, 16.27) * mm});
            skPoint(sketch, "E11.0.3.62", {"position": v(17.78, 16.27) * mm});
            skLineSegment(sketch, "E11.0.3.63", {"start": v(107.44, 16.27) * mm, "end": v(118.57, 16.27) * mm});
            skLineSegment(sketch, "E11.0.3.64", {"start": v(-61.72, 16.27) * mm, "end": v(-50.6, 16.27) * mm});
            skLineSegment(sketch, "E11.0.3.65", {"start": v(-5.33, 16.27) * mm, "end": v(5.79, 16.27) * mm});
            skPoint(sketch, "E11.0.3.66", {"position": v(-123.2, 38.6) * mm});
            skPoint(sketch, "E11.0.3.67", {"position": v(-10.41, 38.6) * mm});
            skPoint(sketch, "E11.0.3.68", {"position": v(102.36, 38.6) * mm});
            skPoint(sketch, "E11.0.3.69", {"position": v(74.17, 38.6) * mm});
            skPoint(sketch, "E11.0.3.70", {"position": v(-10.41, 16.27) * mm});
            skPoint(sketch, "E11.0.3.71", {"position": v(102.36, 16.27) * mm});
            skPoint(sketch, "E11.0.3.72", {"position": v(-38.6, 38.6) * mm});
            skPoint(sketch, "E11.0.3.73", {"position": v(-123.2, 16.27) * mm});
            skPoint(sketch, "E11.0.3.74", {"position": v(-95, 38.6) * mm});
            skLineSegment(sketch, "E11.0.3.75", {"start": v(-38.6, 33.53) * mm, "end": v(-38.6, 21.35) * mm});
            skLineSegment(sketch, "E11.0.3.76", {"start": v(17.78, 33.53) * mm, "end": v(17.78, 21.35) * mm});
            skLineSegment(sketch, "E11.0.3.77", {"start": v(74.17, 33.53) * mm, "end": v(74.17, 21.35) * mm});
            skLineSegment(sketch, "E11.0.3.78", {"start": v(130.56, 33.53) * mm, "end": v(130.56, 21.35) * mm});
            skLineSegment(sketch, "E11.0.3.79", {"start": v(-118.11, 16.27) * mm, "end": v(-106.99, 16.27) * mm});
            skLineSegment(sketch, "E11.0.3.80", {"start": v(-89.92, 38.6) * mm, "end": v(-78.8, 38.6) * mm});
            skLineSegment(sketch, "E11.0.3.81", {"start": v(-78.8, 38.6) * mm, "end": v(-73.71, 33.53) * mm});
            skLineSegment(sketch, "E11.0.3.82", {"start": v(-95, 21.35) * mm, "end": v(-89.92, 16.27) * mm});
            skLineSegment(sketch, "E11.0.3.83", {"start": v(33.98, 38.6) * mm, "end": v(39.06, 33.53) * mm});
            skLineSegment(sketch, "E11.0.3.84", {"start": v(-73.71, 21.35) * mm, "end": v(-78.8, 16.27) * mm});
            skLineSegment(sketch, "E11.0.3.85", {"start": v(-123.2, 33.53) * mm, "end": v(-118.11, 38.6) * mm});
            skLineSegment(sketch, "E11.0.3.86", {"start": v(-106.99, 38.6) * mm, "end": v(-101.9, 33.53) * mm});
            skLineSegment(sketch, "E11.0.3.87", {"start": v(-123.2, 21.35) * mm, "end": v(-118.11, 16.27) * mm});
            skLineSegment(sketch, "E11.0.3.88", {"start": v(-101.9, 21.35) * mm, "end": v(-106.99, 16.27) * mm});
            skLineSegment(sketch, "E11.0.3.89", {"start": v(-45.52, 21.35) * mm, "end": v(-50.6, 16.27) * mm});
            skLineSegment(sketch, "E11.0.3.90", {"start": v(10.87, 21.35) * mm, "end": v(5.79, 16.27) * mm});
            skLineSegment(sketch, "E11.0.3.91", {"start": v(67.26, 21.35) * mm, "end": v(62.18, 16.27) * mm});
            skLineSegment(sketch, "E11.0.3.92", {"start": v(123.65, 21.35) * mm, "end": v(118.57, 16.27) * mm});
            skLineSegment(sketch, "E11.0.3.93", {"start": v(62.18, 38.6) * mm, "end": v(67.26, 33.53) * mm});
            skLineSegment(sketch, "E11.0.3.94", {"start": v(39.06, 21.35) * mm, "end": v(33.98, 16.27) * mm});
            skLineSegment(sketch, "E11.0.3.95", {"start": v(118.57, 38.6) * mm, "end": v(123.65, 33.53) * mm});
            skLineSegment(sketch, "E11.0.3.96", {"start": v(95.45, 21.35) * mm, "end": v(90.37, 16.27) * mm});
            skLineSegment(sketch, "E11.0.3.97", {"start": v(151.84, 21.35) * mm, "end": v(146.76, 16.27) * mm});
            skLineSegment(sketch, "E11.0.3.98", {"start": v(-50.6, 38.6) * mm, "end": v(-45.52, 33.53) * mm});
            skLineSegment(sketch, "E11.0.3.99", {"start": v(5.79, 38.6) * mm, "end": v(10.87, 33.53) * mm});
            skLineSegment(sketch, "E11.0.3.100", {"start": v(-17.32, 21.35) * mm, "end": v(-22.4, 16.27) * mm});
            skLineSegment(sketch, "E11.0.3.101", {"start": v(-38.6, 21.35) * mm, "end": v(-33.53, 16.27) * mm});
            skLineSegment(sketch, "E11.0.3.102", {"start": v(-10.41, 33.53) * mm, "end": v(-5.33, 38.6) * mm});
            skLineSegment(sketch, "E11.0.3.103", {"start": v(-66.8, 33.53) * mm, "end": v(-61.72, 38.6) * mm});
            skLineSegment(sketch, "E11.0.3.104", {"start": v(130.56, 21.35) * mm, "end": v(135.64, 16.27) * mm});
            skLineSegment(sketch, "E11.0.3.105", {"start": v(102.36, 33.53) * mm, "end": v(107.44, 38.6) * mm});
            skLineSegment(sketch, "E11.0.3.106", {"start": v(74.17, 21.35) * mm, "end": v(79.25, 16.27) * mm});
            skLineSegment(sketch, "E11.0.3.107", {"start": v(45.97, 33.53) * mm, "end": v(51.05, 38.6) * mm});
            skLineSegment(sketch, "E11.0.3.108", {"start": v(17.78, 21.35) * mm, "end": v(22.86, 16.27) * mm});
            skLineSegment(sketch, "E11.0.3.109", {"start": v(130.56, 33.53) * mm, "end": v(135.64, 38.6) * mm});
            skLineSegment(sketch, "E11.0.3.110", {"start": v(74.17, 33.53) * mm, "end": v(79.25, 38.6) * mm});
            skLineSegment(sketch, "E11.0.3.111", {"start": v(17.78, 33.53) * mm, "end": v(22.86, 38.6) * mm});
            skLineSegment(sketch, "E11.0.3.112", {"start": v(-95, 33.53) * mm, "end": v(-89.92, 38.6) * mm});
            skLineSegment(sketch, "E11.0.3.113", {"start": v(-38.6, 33.53) * mm, "end": v(-33.53, 38.6) * mm});
            skLineSegment(sketch, "E11.0.3.114", {"start": v(-22.4, 38.6) * mm, "end": v(-17.32, 33.53) * mm});
            skLineSegment(sketch, "E11.0.3.115", {"start": v(-10.41, 21.35) * mm, "end": v(-5.33, 16.27) * mm});
            skLineSegment(sketch, "E11.0.3.116", {"start": v(-66.8, 21.35) * mm, "end": v(-61.72, 16.27) * mm});
            skLineSegment(sketch, "E11.0.3.117", {"start": v(146.76, 38.6) * mm, "end": v(151.84, 33.53) * mm});
            skLineSegment(sketch, "E11.0.3.118", {"start": v(102.36, 21.35) * mm, "end": v(107.44, 16.27) * mm});
            skLineSegment(sketch, "E11.0.3.119", {"start": v(90.37, 38.6) * mm, "end": v(95.45, 33.53) * mm});
            skLineSegment(sketch, "E11.0.3.120", {"start": v(45.97, 21.35) * mm, "end": v(51.05, 16.27) * mm});
            skPoint(sketch, "E11.0.4.0", {"position": v(-73.71, 10.41) * mm});
            skLineSegment(sketch, "E11.0.4.1", {"start": v(102.36, 5.33) * mm, "end": v(102.36, -6.84) * mm});
            skLineSegment(sketch, "E11.0.4.2", {"start": v(45.97, 5.33) * mm, "end": v(45.97, -6.84) * mm});
            skPoint(sketch, "E11.0.4.3", {"position": v(39.06, 10.41) * mm});
            skLineSegment(sketch, "E11.0.4.4", {"start": v(-66.8, 5.33) * mm, "end": v(-66.8, -6.84) * mm});
            skLineSegment(sketch, "E11.0.4.5", {"start": v(-95, 5.33) * mm, "end": v(-95, -6.84) * mm});
            skLineSegment(sketch, "E11.0.4.6", {"start": v(-73.71, 5.33) * mm, "end": v(-73.71, -6.84) * mm});
            skLineSegment(sketch, "E11.0.4.7", {"start": v(-123.2, 5.33) * mm, "end": v(-123.2, -6.84) * mm});
            skLineSegment(sketch, "E11.0.4.8", {"start": v(-101.9, 5.33) * mm, "end": v(-101.9, -6.84) * mm});
            skPoint(sketch, "E11.0.4.9", {"position": v(130.56, -11.92) * mm});
            skPoint(sketch, "E11.0.4.10", {"position": v(67.26, 10.41) * mm});
            skPoint(sketch, "E11.0.4.11", {"position": v(-66.8, -11.92) * mm});
            skPoint(sketch, "E11.0.4.12", {"position": v(10.87, 10.41) * mm});
            skPoint(sketch, "E11.0.4.13", {"position": v(-101.9, -11.92) * mm});
            skPoint(sketch, "E11.0.4.14", {"position": v(45.97, -11.92) * mm});
            skLineSegment(sketch, "E11.0.4.15", {"start": v(-118.11, 10.41) * mm, "end": v(-106.99, 10.41) * mm});
            skPoint(sketch, "E11.0.4.16", {"position": v(-45.52, 10.41) * mm});
            skPoint(sketch, "E11.0.4.17", {"position": v(151.84, 10.41) * mm});
            skPoint(sketch, "E11.0.4.18", {"position": v(123.65, 10.41) * mm});
            skLineSegment(sketch, "E11.0.4.19", {"start": v(151.84, 5.33) * mm, "end": v(151.84, -6.84) * mm});
            skLineSegment(sketch, "E11.0.4.20", {"start": v(95.45, 5.33) * mm, "end": v(95.45, -6.84) * mm});
            skLineSegment(sketch, "E11.0.4.21", {"start": v(39.06, 5.33) * mm, "end": v(39.06, -6.84) * mm});
            skLineSegment(sketch, "E11.0.4.22", {"start": v(-17.32, 5.33) * mm, "end": v(-17.32, -6.84) * mm});
            skPoint(sketch, "E11.0.4.23", {"position": v(74.17, -11.92) * mm});
            skPoint(sketch, "E11.0.4.24", {"position": v(-38.6, -11.92) * mm});
            skLineSegment(sketch, "E11.0.4.25", {"start": v(-10.41, 5.33) * mm, "end": v(-10.41, -6.84) * mm});
            skLineSegment(sketch, "E11.0.4.26", {"start": v(-89.92, -11.92) * mm, "end": v(-78.8, -11.92) * mm});
            skLineSegment(sketch, "E11.0.4.27", {"start": v(-45.52, 5.33) * mm, "end": v(-45.52, -6.84) * mm});
            skLineSegment(sketch, "E11.0.4.28", {"start": v(10.87, 5.33) * mm, "end": v(10.87, -6.84) * mm});
            skPoint(sketch, "E11.0.4.29", {"position": v(-17.32, 10.41) * mm});
            skPoint(sketch, "E11.0.4.30", {"position": v(95.45, 10.41) * mm});
            skPoint(sketch, "E11.0.4.31", {"position": v(95.45, -11.92) * mm});
            skPoint(sketch, "E11.0.4.32", {"position": v(151.84, -11.92) * mm});
            skPoint(sketch, "E11.0.4.33", {"position": v(-73.71, -11.92) * mm});
            skPoint(sketch, "E11.0.4.34", {"position": v(39.06, -11.92) * mm});
            skLineSegment(sketch, "E11.0.4.35", {"start": v(67.26, 5.33) * mm, "end": v(67.26, -6.84) * mm});
            skLineSegment(sketch, "E11.0.4.36", {"start": v(123.65, 5.33) * mm, "end": v(123.65, -6.84) * mm});
            skLineSegment(sketch, "E11.0.4.37", {"start": v(-123.2, -11.92) * mm, "end": v(-95, -11.92) * mm, "construction": true});
            skPoint(sketch, "E11.0.4.38", {"position": v(130.56, 10.41) * mm});
            skPoint(sketch, "E11.0.4.39", {"position": v(45.97, 10.41) * mm});
            skLineSegment(sketch, "E11.0.4.40", {"start": v(51.05, 10.41) * mm, "end": v(62.18, 10.41) * mm});
            skPoint(sketch, "E11.0.4.41", {"position": v(-66.8, 10.41) * mm});
            skLineSegment(sketch, "E11.0.4.42", {"start": v(107.44, 10.41) * mm, "end": v(118.57, 10.41) * mm});
            skLineSegment(sketch, "E11.0.4.43", {"start": v(135.64, 10.41) * mm, "end": v(146.76, 10.41) * mm});
            skLineSegment(sketch, "E11.0.4.44", {"start": v(79.25, 10.41) * mm, "end": v(90.37, 10.41) * mm});
            skLineSegment(sketch, "E11.0.4.45", {"start": v(22.86, 10.41) * mm, "end": v(33.98, 10.41) * mm});
            skLineSegment(sketch, "E11.0.4.46", {"start": v(-33.53, 10.41) * mm, "end": v(-22.4, 10.41) * mm});
            skLineSegment(sketch, "E11.0.4.47", {"start": v(-61.72, 10.41) * mm, "end": v(-50.6, 10.41) * mm});
            skPoint(sketch, "E11.0.4.48", {"position": v(-17.32, -11.92) * mm});
            skLineSegment(sketch, "E11.0.4.49", {"start": v(-5.33, 10.41) * mm, "end": v(5.79, 10.41) * mm});
            skLineSegment(sketch, "E11.0.4.50", {"start": v(-33.53, -11.92) * mm, "end": v(-22.4, -11.92) * mm});
            skLineSegment(sketch, "E11.0.4.51", {"start": v(22.86, -11.92) * mm, "end": v(33.98, -11.92) * mm});
            skPoint(sketch, "E11.0.4.52", {"position": v(17.78, 10.41) * mm});
            skLineSegment(sketch, "E11.0.4.53", {"start": v(79.25, -11.92) * mm, "end": v(90.37, -11.92) * mm});
            skLineSegment(sketch, "E11.0.4.54", {"start": v(135.64, -11.92) * mm, "end": v(146.76, -11.92) * mm});
            skPoint(sketch, "E11.0.4.55", {"position": v(67.26, -11.92) * mm});
            skPoint(sketch, "E11.0.4.56", {"position": v(-101.9, 10.41) * mm});
            skPoint(sketch, "E11.0.4.57", {"position": v(10.87, -11.92) * mm});
            skPoint(sketch, "E11.0.4.58", {"position": v(123.65, -11.92) * mm});
            skPoint(sketch, "E11.0.4.59", {"position": v(-45.52, -11.92) * mm});
            skPoint(sketch, "E11.0.4.60", {"position": v(-95, -11.92) * mm});
            skLineSegment(sketch, "E11.0.4.61", {"start": v(51.05, -11.92) * mm, "end": v(62.18, -11.92) * mm});
            skPoint(sketch, "E11.0.4.62", {"position": v(17.78, -11.92) * mm});
            skLineSegment(sketch, "E11.0.4.63", {"start": v(107.44, -11.92) * mm, "end": v(118.57, -11.92) * mm});
            skLineSegment(sketch, "E11.0.4.64", {"start": v(-61.72, -11.92) * mm, "end": v(-50.6, -11.92) * mm});
            skLineSegment(sketch, "E11.0.4.65", {"start": v(-5.33, -11.92) * mm, "end": v(5.79, -11.92) * mm});
            skPoint(sketch, "E11.0.4.66", {"position": v(-123.2, 10.41) * mm});
            skPoint(sketch, "E11.0.4.67", {"position": v(-10.41, 10.41) * mm});
            skPoint(sketch, "E11.0.4.68", {"position": v(102.36, 10.41) * mm});
            skPoint(sketch, "E11.0.4.69", {"position": v(74.17, 10.41) * mm});
            skPoint(sketch, "E11.0.4.70", {"position": v(-10.41, -11.92) * mm});
            skPoint(sketch, "E11.0.4.71", {"position": v(102.36, -11.92) * mm});
            skPoint(sketch, "E11.0.4.72", {"position": v(-38.6, 10.41) * mm});
            skPoint(sketch, "E11.0.4.73", {"position": v(-123.2, -11.92) * mm});
            skPoint(sketch, "E11.0.4.74", {"position": v(-95, 10.41) * mm});
            skLineSegment(sketch, "E11.0.4.75", {"start": v(-38.6, 5.33) * mm, "end": v(-38.6, -6.84) * mm});
            skLineSegment(sketch, "E11.0.4.76", {"start": v(17.78, 5.33) * mm, "end": v(17.78, -6.84) * mm});
            skLineSegment(sketch, "E11.0.4.77", {"start": v(74.17, 5.33) * mm, "end": v(74.17, -6.84) * mm});
            skLineSegment(sketch, "E11.0.4.78", {"start": v(130.56, 5.33) * mm, "end": v(130.56, -6.84) * mm});
            skLineSegment(sketch, "E11.0.4.79", {"start": v(-118.11, -11.92) * mm, "end": v(-106.99, -11.92) * mm});
            skLineSegment(sketch, "E11.0.4.80", {"start": v(-89.92, 10.41) * mm, "end": v(-78.8, 10.41) * mm});
            skLineSegment(sketch, "E11.0.4.81", {"start": v(-78.8, 10.41) * mm, "end": v(-73.71, 5.33) * mm});
            skLineSegment(sketch, "E11.0.4.82", {"start": v(-95, -6.84) * mm, "end": v(-89.92, -11.92) * mm});
            skLineSegment(sketch, "E11.0.4.83", {"start": v(33.98, 10.41) * mm, "end": v(39.06, 5.33) * mm});
            skLineSegment(sketch, "E11.0.4.84", {"start": v(-73.71, -6.84) * mm, "end": v(-78.8, -11.92) * mm});
            skLineSegment(sketch, "E11.0.4.85", {"start": v(-123.2, 5.33) * mm, "end": v(-118.11, 10.41) * mm});
            skLineSegment(sketch, "E11.0.4.86", {"start": v(-106.99, 10.41) * mm, "end": v(-101.9, 5.33) * mm});
            skLineSegment(sketch, "E11.0.4.87", {"start": v(-123.2, -6.84) * mm, "end": v(-118.11, -11.92) * mm});
            skLineSegment(sketch, "E11.0.4.88", {"start": v(-101.9, -6.84) * mm, "end": v(-106.99, -11.92) * mm});
            skLineSegment(sketch, "E11.0.4.89", {"start": v(-45.52, -6.84) * mm, "end": v(-50.6, -11.92) * mm});
            skLineSegment(sketch, "E11.0.4.90", {"start": v(10.87, -6.84) * mm, "end": v(5.79, -11.92) * mm});
            skLineSegment(sketch, "E11.0.4.91", {"start": v(67.26, -6.84) * mm, "end": v(62.18, -11.92) * mm});
            skLineSegment(sketch, "E11.0.4.92", {"start": v(123.65, -6.84) * mm, "end": v(118.57, -11.92) * mm});
            skLineSegment(sketch, "E11.0.4.93", {"start": v(62.18, 10.41) * mm, "end": v(67.26, 5.33) * mm});
            skLineSegment(sketch, "E11.0.4.94", {"start": v(39.06, -6.84) * mm, "end": v(33.98, -11.92) * mm});
            skLineSegment(sketch, "E11.0.4.95", {"start": v(118.57, 10.41) * mm, "end": v(123.65, 5.33) * mm});
            skLineSegment(sketch, "E11.0.4.96", {"start": v(95.45, -6.84) * mm, "end": v(90.37, -11.92) * mm});
            skLineSegment(sketch, "E11.0.4.97", {"start": v(151.84, -6.84) * mm, "end": v(146.76, -11.92) * mm});
            skLineSegment(sketch, "E11.0.4.98", {"start": v(-50.6, 10.41) * mm, "end": v(-45.52, 5.33) * mm});
            skLineSegment(sketch, "E11.0.4.99", {"start": v(5.79, 10.41) * mm, "end": v(10.87, 5.33) * mm});
            skLineSegment(sketch, "E11.0.4.100", {"start": v(-17.32, -6.84) * mm, "end": v(-22.4, -11.92) * mm});
            skLineSegment(sketch, "E11.0.4.101", {"start": v(-38.6, -6.84) * mm, "end": v(-33.53, -11.92) * mm});
            skLineSegment(sketch, "E11.0.4.102", {"start": v(-10.41, 5.33) * mm, "end": v(-5.33, 10.41) * mm});
            skLineSegment(sketch, "E11.0.4.103", {"start": v(-66.8, 5.33) * mm, "end": v(-61.72, 10.41) * mm});
            skLineSegment(sketch, "E11.0.4.104", {"start": v(130.56, -6.84) * mm, "end": v(135.64, -11.92) * mm});
            skLineSegment(sketch, "E11.0.4.105", {"start": v(102.36, 5.33) * mm, "end": v(107.44, 10.41) * mm});
            skLineSegment(sketch, "E11.0.4.106", {"start": v(74.17, -6.84) * mm, "end": v(79.25, -11.92) * mm});
            skLineSegment(sketch, "E11.0.4.107", {"start": v(45.97, 5.33) * mm, "end": v(51.05, 10.41) * mm});
            skLineSegment(sketch, "E11.0.4.108", {"start": v(17.78, -6.84) * mm, "end": v(22.86, -11.92) * mm});
            skLineSegment(sketch, "E11.0.4.109", {"start": v(130.56, 5.33) * mm, "end": v(135.64, 10.41) * mm});
            skLineSegment(sketch, "E11.0.4.110", {"start": v(74.17, 5.33) * mm, "end": v(79.25, 10.41) * mm});
            skLineSegment(sketch, "E11.0.4.111", {"start": v(17.78, 5.33) * mm, "end": v(22.86, 10.41) * mm});
            skLineSegment(sketch, "E11.0.4.112", {"start": v(-95, 5.33) * mm, "end": v(-89.92, 10.41) * mm});
            skLineSegment(sketch, "E11.0.4.113", {"start": v(-38.6, 5.33) * mm, "end": v(-33.53, 10.41) * mm});
            skLineSegment(sketch, "E11.0.4.114", {"start": v(-22.4, 10.41) * mm, "end": v(-17.32, 5.33) * mm});
            skLineSegment(sketch, "E11.0.4.115", {"start": v(-10.41, -6.84) * mm, "end": v(-5.33, -11.92) * mm});
            skLineSegment(sketch, "E11.0.4.116", {"start": v(-66.8, -6.84) * mm, "end": v(-61.72, -11.92) * mm});
            skLineSegment(sketch, "E11.0.4.117", {"start": v(146.76, 10.41) * mm, "end": v(151.84, 5.33) * mm});
            skLineSegment(sketch, "E11.0.4.118", {"start": v(102.36, -6.84) * mm, "end": v(107.44, -11.92) * mm});
            skLineSegment(sketch, "E11.0.4.119", {"start": v(90.37, 10.41) * mm, "end": v(95.45, 5.33) * mm});
            skLineSegment(sketch, "E11.0.4.120", {"start": v(45.97, -6.84) * mm, "end": v(51.05, -11.92) * mm});
            skPoint(sketch, "E11.0.5.0", {"position": v(-73.71, -17.78) * mm});
            skLineSegment(sketch, "E11.0.5.1", {"start": v(102.36, -22.86) * mm, "end": v(102.36, -35.04) * mm});
            skLineSegment(sketch, "E11.0.5.2", {"start": v(45.97, -22.86) * mm, "end": v(45.97, -35.04) * mm});
            skPoint(sketch, "E11.0.5.3", {"position": v(39.06, -17.78) * mm});
            skLineSegment(sketch, "E11.0.5.4", {"start": v(-66.8, -22.86) * mm, "end": v(-66.8, -35.04) * mm});
            skLineSegment(sketch, "E11.0.5.5", {"start": v(-95, -22.86) * mm, "end": v(-95, -35.04) * mm});
            skLineSegment(sketch, "E11.0.5.6", {"start": v(-73.71, -22.86) * mm, "end": v(-73.71, -35.04) * mm});
            skLineSegment(sketch, "E11.0.5.7", {"start": v(-123.2, -22.86) * mm, "end": v(-123.2, -35.04) * mm});
            skLineSegment(sketch, "E11.0.5.8", {"start": v(-101.9, -22.86) * mm, "end": v(-101.9, -35.04) * mm});
            skPoint(sketch, "E11.0.5.9", {"position": v(130.56, -40.12) * mm});
            skPoint(sketch, "E11.0.5.10", {"position": v(67.26, -17.78) * mm});
            skPoint(sketch, "E11.0.5.11", {"position": v(-66.8, -40.12) * mm});
            skPoint(sketch, "E11.0.5.12", {"position": v(10.87, -17.78) * mm});
            skPoint(sketch, "E11.0.5.13", {"position": v(-101.9, -40.12) * mm});
            skPoint(sketch, "E11.0.5.14", {"position": v(45.97, -40.12) * mm});
            skLineSegment(sketch, "E11.0.5.15", {"start": v(-118.11, -17.78) * mm, "end": v(-106.99, -17.78) * mm});
            skPoint(sketch, "E11.0.5.16", {"position": v(-45.52, -17.78) * mm});
            skPoint(sketch, "E11.0.5.17", {"position": v(151.84, -17.78) * mm});
            skPoint(sketch, "E11.0.5.18", {"position": v(123.65, -17.78) * mm});
            skLineSegment(sketch, "E11.0.5.19", {"start": v(151.84, -22.86) * mm, "end": v(151.84, -35.04) * mm});
            skLineSegment(sketch, "E11.0.5.20", {"start": v(95.45, -22.86) * mm, "end": v(95.45, -35.04) * mm});
            skLineSegment(sketch, "E11.0.5.21", {"start": v(39.06, -22.86) * mm, "end": v(39.06, -35.04) * mm});
            skLineSegment(sketch, "E11.0.5.22", {"start": v(-17.32, -22.86) * mm, "end": v(-17.32, -35.04) * mm});
            skPoint(sketch, "E11.0.5.23", {"position": v(74.17, -40.12) * mm});
            skPoint(sketch, "E11.0.5.24", {"position": v(-38.6, -40.12) * mm});
            skLineSegment(sketch, "E11.0.5.25", {"start": v(-10.41, -22.86) * mm, "end": v(-10.41, -35.04) * mm});
            skLineSegment(sketch, "E11.0.5.26", {"start": v(-89.92, -40.12) * mm, "end": v(-78.8, -40.12) * mm});
            skLineSegment(sketch, "E11.0.5.27", {"start": v(-45.52, -22.86) * mm, "end": v(-45.52, -35.04) * mm});
            skLineSegment(sketch, "E11.0.5.28", {"start": v(10.87, -22.86) * mm, "end": v(10.87, -35.04) * mm});
            skPoint(sketch, "E11.0.5.29", {"position": v(-17.32, -17.78) * mm});
            skPoint(sketch, "E11.0.5.30", {"position": v(95.45, -17.78) * mm});
            skPoint(sketch, "E11.0.5.31", {"position": v(95.45, -40.12) * mm});
            skPoint(sketch, "E11.0.5.32", {"position": v(151.84, -40.12) * mm});
            skPoint(sketch, "E11.0.5.33", {"position": v(-73.71, -40.12) * mm});
            skPoint(sketch, "E11.0.5.34", {"position": v(39.06, -40.12) * mm});
            skLineSegment(sketch, "E11.0.5.35", {"start": v(67.26, -22.86) * mm, "end": v(67.26, -35.04) * mm});
            skLineSegment(sketch, "E11.0.5.36", {"start": v(123.65, -22.86) * mm, "end": v(123.65, -35.04) * mm});
            skLineSegment(sketch, "E11.0.5.37", {"start": v(-123.2, -40.12) * mm, "end": v(-95, -40.12) * mm, "construction": true});
            skPoint(sketch, "E11.0.5.38", {"position": v(130.56, -17.78) * mm});
            skPoint(sketch, "E11.0.5.39", {"position": v(45.97, -17.78) * mm});
            skLineSegment(sketch, "E11.0.5.40", {"start": v(51.05, -17.78) * mm, "end": v(62.18, -17.78) * mm});
            skPoint(sketch, "E11.0.5.41", {"position": v(-66.8, -17.78) * mm});
            skLineSegment(sketch, "E11.0.5.42", {"start": v(107.44, -17.78) * mm, "end": v(118.57, -17.78) * mm});
            skLineSegment(sketch, "E11.0.5.43", {"start": v(135.64, -17.78) * mm, "end": v(146.76, -17.78) * mm});
            skLineSegment(sketch, "E11.0.5.44", {"start": v(79.25, -17.78) * mm, "end": v(90.37, -17.78) * mm});
            skLineSegment(sketch, "E11.0.5.45", {"start": v(22.86, -17.78) * mm, "end": v(33.98, -17.78) * mm});
            skLineSegment(sketch, "E11.0.5.46", {"start": v(-33.53, -17.78) * mm, "end": v(-22.4, -17.78) * mm});
            skLineSegment(sketch, "E11.0.5.47", {"start": v(-61.72, -17.78) * mm, "end": v(-50.6, -17.78) * mm});
            skPoint(sketch, "E11.0.5.48", {"position": v(-17.32, -40.12) * mm});
            skLineSegment(sketch, "E11.0.5.49", {"start": v(-5.33, -17.78) * mm, "end": v(5.79, -17.78) * mm});
            skLineSegment(sketch, "E11.0.5.50", {"start": v(-33.53, -40.12) * mm, "end": v(-22.4, -40.12) * mm});
            skLineSegment(sketch, "E11.0.5.51", {"start": v(22.86, -40.12) * mm, "end": v(33.98, -40.12) * mm});
            skPoint(sketch, "E11.0.5.52", {"position": v(17.78, -17.78) * mm});
            skLineSegment(sketch, "E11.0.5.53", {"start": v(79.25, -40.12) * mm, "end": v(90.37, -40.12) * mm});
            skLineSegment(sketch, "E11.0.5.54", {"start": v(135.64, -40.12) * mm, "end": v(146.76, -40.12) * mm});
            skPoint(sketch, "E11.0.5.55", {"position": v(67.26, -40.12) * mm});
            skPoint(sketch, "E11.0.5.56", {"position": v(-101.9, -17.78) * mm});
            skPoint(sketch, "E11.0.5.57", {"position": v(10.87, -40.12) * mm});
            skPoint(sketch, "E11.0.5.58", {"position": v(123.65, -40.12) * mm});
            skPoint(sketch, "E11.0.5.59", {"position": v(-45.52, -40.12) * mm});
            skPoint(sketch, "E11.0.5.60", {"position": v(-95, -40.12) * mm});
            skLineSegment(sketch, "E11.0.5.61", {"start": v(51.05, -40.12) * mm, "end": v(62.18, -40.12) * mm});
            skPoint(sketch, "E11.0.5.62", {"position": v(17.78, -40.12) * mm});
            skLineSegment(sketch, "E11.0.5.63", {"start": v(107.44, -40.12) * mm, "end": v(118.57, -40.12) * mm});
            skLineSegment(sketch, "E11.0.5.64", {"start": v(-61.72, -40.12) * mm, "end": v(-50.6, -40.12) * mm});
            skLineSegment(sketch, "E11.0.5.65", {"start": v(-5.33, -40.12) * mm, "end": v(5.79, -40.12) * mm});
            skPoint(sketch, "E11.0.5.66", {"position": v(-123.2, -17.78) * mm});
            skPoint(sketch, "E11.0.5.67", {"position": v(-10.41, -17.78) * mm});
            skPoint(sketch, "E11.0.5.68", {"position": v(102.36, -17.78) * mm});
            skPoint(sketch, "E11.0.5.69", {"position": v(74.17, -17.78) * mm});
            skPoint(sketch, "E11.0.5.70", {"position": v(-10.41, -40.12) * mm});
            skPoint(sketch, "E11.0.5.71", {"position": v(102.36, -40.12) * mm});
            skPoint(sketch, "E11.0.5.72", {"position": v(-38.6, -17.78) * mm});
            skPoint(sketch, "E11.0.5.73", {"position": v(-123.2, -40.12) * mm});
            skPoint(sketch, "E11.0.5.74", {"position": v(-95, -17.78) * mm});
            skLineSegment(sketch, "E11.0.5.75", {"start": v(-38.6, -22.86) * mm, "end": v(-38.6, -35.04) * mm});
            skLineSegment(sketch, "E11.0.5.76", {"start": v(17.78, -22.86) * mm, "end": v(17.78, -35.04) * mm});
            skLineSegment(sketch, "E11.0.5.77", {"start": v(74.17, -22.86) * mm, "end": v(74.17, -35.04) * mm});
            skLineSegment(sketch, "E11.0.5.78", {"start": v(130.56, -22.86) * mm, "end": v(130.56, -35.04) * mm});
            skLineSegment(sketch, "E11.0.5.79", {"start": v(-118.11, -40.12) * mm, "end": v(-106.99, -40.12) * mm});
            skLineSegment(sketch, "E11.0.5.80", {"start": v(-89.92, -17.78) * mm, "end": v(-78.8, -17.78) * mm});
            skLineSegment(sketch, "E11.0.5.81", {"start": v(-78.8, -17.78) * mm, "end": v(-73.71, -22.86) * mm});
            skLineSegment(sketch, "E11.0.5.82", {"start": v(-95, -35.04) * mm, "end": v(-89.92, -40.12) * mm});
            skLineSegment(sketch, "E11.0.5.83", {"start": v(33.98, -17.78) * mm, "end": v(39.06, -22.86) * mm});
            skLineSegment(sketch, "E11.0.5.84", {"start": v(-73.71, -35.04) * mm, "end": v(-78.8, -40.12) * mm});
            skLineSegment(sketch, "E11.0.5.85", {"start": v(-123.2, -22.86) * mm, "end": v(-118.11, -17.78) * mm});
            skLineSegment(sketch, "E11.0.5.86", {"start": v(-106.99, -17.78) * mm, "end": v(-101.9, -22.86) * mm});
            skLineSegment(sketch, "E11.0.5.87", {"start": v(-123.2, -35.04) * mm, "end": v(-118.11, -40.12) * mm});
            skLineSegment(sketch, "E11.0.5.88", {"start": v(-101.9, -35.04) * mm, "end": v(-106.99, -40.12) * mm});
            skLineSegment(sketch, "E11.0.5.89", {"start": v(-45.52, -35.04) * mm, "end": v(-50.6, -40.12) * mm});
            skLineSegment(sketch, "E11.0.5.90", {"start": v(10.87, -35.04) * mm, "end": v(5.79, -40.12) * mm});
            skLineSegment(sketch, "E11.0.5.91", {"start": v(67.26, -35.04) * mm, "end": v(62.18, -40.12) * mm});
            skLineSegment(sketch, "E11.0.5.92", {"start": v(123.65, -35.04) * mm, "end": v(118.57, -40.12) * mm});
            skLineSegment(sketch, "E11.0.5.93", {"start": v(62.18, -17.78) * mm, "end": v(67.26, -22.86) * mm});
            skLineSegment(sketch, "E11.0.5.94", {"start": v(39.06, -35.04) * mm, "end": v(33.98, -40.12) * mm});
            skLineSegment(sketch, "E11.0.5.95", {"start": v(118.57, -17.78) * mm, "end": v(123.65, -22.86) * mm});
            skLineSegment(sketch, "E11.0.5.96", {"start": v(95.45, -35.04) * mm, "end": v(90.37, -40.12) * mm});
            skLineSegment(sketch, "E11.0.5.97", {"start": v(151.84, -35.04) * mm, "end": v(146.76, -40.12) * mm});
            skLineSegment(sketch, "E11.0.5.98", {"start": v(-50.6, -17.78) * mm, "end": v(-45.52, -22.86) * mm});
            skLineSegment(sketch, "E11.0.5.99", {"start": v(5.79, -17.78) * mm, "end": v(10.87, -22.86) * mm});
            skLineSegment(sketch, "E11.0.5.100", {"start": v(-17.32, -35.04) * mm, "end": v(-22.4, -40.12) * mm});
            skLineSegment(sketch, "E11.0.5.101", {"start": v(-38.6, -35.04) * mm, "end": v(-33.53, -40.12) * mm});
            skLineSegment(sketch, "E11.0.5.102", {"start": v(-10.41, -22.86) * mm, "end": v(-5.33, -17.78) * mm});
            skLineSegment(sketch, "E11.0.5.103", {"start": v(-66.8, -22.86) * mm, "end": v(-61.72, -17.78) * mm});
            skLineSegment(sketch, "E11.0.5.104", {"start": v(130.56, -35.04) * mm, "end": v(135.64, -40.12) * mm});
            skLineSegment(sketch, "E11.0.5.105", {"start": v(102.36, -22.86) * mm, "end": v(107.44, -17.78) * mm});
            skLineSegment(sketch, "E11.0.5.106", {"start": v(74.17, -35.04) * mm, "end": v(79.25, -40.12) * mm});
            skLineSegment(sketch, "E11.0.5.107", {"start": v(45.97, -22.86) * mm, "end": v(51.05, -17.78) * mm});
            skLineSegment(sketch, "E11.0.5.108", {"start": v(17.78, -35.04) * mm, "end": v(22.86, -40.12) * mm});
            skLineSegment(sketch, "E11.0.5.109", {"start": v(130.56, -22.86) * mm, "end": v(135.64, -17.78) * mm});
            skLineSegment(sketch, "E11.0.5.110", {"start": v(74.17, -22.86) * mm, "end": v(79.25, -17.78) * mm});
            skLineSegment(sketch, "E11.0.5.111", {"start": v(17.78, -22.86) * mm, "end": v(22.86, -17.78) * mm});
            skLineSegment(sketch, "E11.0.5.112", {"start": v(-95, -22.86) * mm, "end": v(-89.92, -17.78) * mm});
            skLineSegment(sketch, "E11.0.5.113", {"start": v(-38.6, -22.86) * mm, "end": v(-33.53, -17.78) * mm});
            skLineSegment(sketch, "E11.0.5.114", {"start": v(-22.4, -17.78) * mm, "end": v(-17.32, -22.86) * mm});
            skLineSegment(sketch, "E11.0.5.115", {"start": v(-10.41, -35.04) * mm, "end": v(-5.33, -40.12) * mm});
            skLineSegment(sketch, "E11.0.5.116", {"start": v(-66.8, -35.04) * mm, "end": v(-61.72, -40.12) * mm});
            skLineSegment(sketch, "E11.0.5.117", {"start": v(146.76, -17.78) * mm, "end": v(151.84, -22.86) * mm});
            skLineSegment(sketch, "E11.0.5.118", {"start": v(102.36, -35.04) * mm, "end": v(107.44, -40.12) * mm});
            skLineSegment(sketch, "E11.0.5.119", {"start": v(90.37, -17.78) * mm, "end": v(95.45, -22.86) * mm});
            skLineSegment(sketch, "E11.0.5.120", {"start": v(45.97, -35.04) * mm, "end": v(51.05, -40.12) * mm});
            skPoint(sketch, "E11.0.6.0", {"position": v(-73.71, -45.97) * mm});
            skLineSegment(sketch, "E11.0.6.1", {"start": v(102.36, -51.05) * mm, "end": v(102.36, -63.23) * mm});
            skLineSegment(sketch, "E11.0.6.2", {"start": v(45.97, -51.05) * mm, "end": v(45.97, -63.23) * mm});
            skPoint(sketch, "E11.0.6.3", {"position": v(39.06, -45.97) * mm});
            skLineSegment(sketch, "E11.0.6.4", {"start": v(-66.8, -51.05) * mm, "end": v(-66.8, -63.23) * mm});
            skLineSegment(sketch, "E11.0.6.5", {"start": v(-95, -51.05) * mm, "end": v(-95, -63.23) * mm});
            skLineSegment(sketch, "E11.0.6.6", {"start": v(-73.71, -51.05) * mm, "end": v(-73.71, -63.23) * mm});
            skLineSegment(sketch, "E11.0.6.7", {"start": v(-123.2, -51.05) * mm, "end": v(-123.2, -63.23) * mm});
            skLineSegment(sketch, "E11.0.6.8", {"start": v(-101.9, -51.05) * mm, "end": v(-101.9, -63.23) * mm});
            skPoint(sketch, "E11.0.6.9", {"position": v(130.56, -68.3) * mm});
            skPoint(sketch, "E11.0.6.10", {"position": v(67.26, -45.97) * mm});
            skPoint(sketch, "E11.0.6.11", {"position": v(-66.8, -68.3) * mm});
            skPoint(sketch, "E11.0.6.12", {"position": v(10.87, -45.97) * mm});
            skPoint(sketch, "E11.0.6.13", {"position": v(-101.9, -68.3) * mm});
            skPoint(sketch, "E11.0.6.14", {"position": v(45.97, -68.3) * mm});
            skLineSegment(sketch, "E11.0.6.15", {"start": v(-118.11, -45.97) * mm, "end": v(-106.99, -45.97) * mm});
            skPoint(sketch, "E11.0.6.16", {"position": v(-45.52, -45.97) * mm});
            skPoint(sketch, "E11.0.6.17", {"position": v(151.84, -45.97) * mm});
            skPoint(sketch, "E11.0.6.18", {"position": v(123.65, -45.97) * mm});
            skLineSegment(sketch, "E11.0.6.19", {"start": v(151.84, -51.05) * mm, "end": v(151.84, -63.23) * mm});
            skLineSegment(sketch, "E11.0.6.20", {"start": v(95.45, -51.05) * mm, "end": v(95.45, -63.23) * mm});
            skLineSegment(sketch, "E11.0.6.21", {"start": v(39.06, -51.05) * mm, "end": v(39.06, -63.23) * mm});
            skLineSegment(sketch, "E11.0.6.22", {"start": v(-17.32, -51.05) * mm, "end": v(-17.32, -63.23) * mm});
            skPoint(sketch, "E11.0.6.23", {"position": v(74.17, -68.3) * mm});
            skPoint(sketch, "E11.0.6.24", {"position": v(-38.6, -68.3) * mm});
            skLineSegment(sketch, "E11.0.6.25", {"start": v(-10.41, -51.05) * mm, "end": v(-10.41, -63.23) * mm});
            skLineSegment(sketch, "E11.0.6.26", {"start": v(-89.92, -68.3) * mm, "end": v(-78.8, -68.3) * mm});
            skLineSegment(sketch, "E11.0.6.27", {"start": v(-45.52, -51.05) * mm, "end": v(-45.52, -63.23) * mm});
            skLineSegment(sketch, "E11.0.6.28", {"start": v(10.87, -51.05) * mm, "end": v(10.87, -63.23) * mm});
            skPoint(sketch, "E11.0.6.29", {"position": v(-17.32, -45.97) * mm});
            skPoint(sketch, "E11.0.6.30", {"position": v(95.45, -45.97) * mm});
            skPoint(sketch, "E11.0.6.31", {"position": v(95.45, -68.3) * mm});
            skPoint(sketch, "E11.0.6.32", {"position": v(151.84, -68.3) * mm});
            skPoint(sketch, "E11.0.6.33", {"position": v(-73.71, -68.3) * mm});
            skPoint(sketch, "E11.0.6.34", {"position": v(39.06, -68.3) * mm});
            skLineSegment(sketch, "E11.0.6.35", {"start": v(67.26, -51.05) * mm, "end": v(67.26, -63.23) * mm});
            skLineSegment(sketch, "E11.0.6.36", {"start": v(123.65, -51.05) * mm, "end": v(123.65, -63.23) * mm});
            skLineSegment(sketch, "E11.0.6.37", {"start": v(-123.2, -68.3) * mm, "end": v(-95, -68.3) * mm, "construction": true});
            skPoint(sketch, "E11.0.6.38", {"position": v(130.56, -45.97) * mm});
            skPoint(sketch, "E11.0.6.39", {"position": v(45.97, -45.97) * mm});
            skLineSegment(sketch, "E11.0.6.40", {"start": v(51.05, -45.97) * mm, "end": v(62.18, -45.97) * mm});
            skPoint(sketch, "E11.0.6.41", {"position": v(-66.8, -45.97) * mm});
            skLineSegment(sketch, "E11.0.6.42", {"start": v(107.44, -45.97) * mm, "end": v(118.57, -45.97) * mm});
            skLineSegment(sketch, "E11.0.6.43", {"start": v(135.64, -45.97) * mm, "end": v(146.76, -45.97) * mm});
            skLineSegment(sketch, "E11.0.6.44", {"start": v(79.25, -45.97) * mm, "end": v(90.37, -45.97) * mm});
            skLineSegment(sketch, "E11.0.6.45", {"start": v(22.86, -45.97) * mm, "end": v(33.98, -45.97) * mm});
            skLineSegment(sketch, "E11.0.6.46", {"start": v(-33.53, -45.97) * mm, "end": v(-22.4, -45.97) * mm});
            skLineSegment(sketch, "E11.0.6.47", {"start": v(-61.72, -45.97) * mm, "end": v(-50.6, -45.97) * mm});
            skPoint(sketch, "E11.0.6.48", {"position": v(-17.32, -68.3) * mm});
            skLineSegment(sketch, "E11.0.6.49", {"start": v(-5.33, -45.97) * mm, "end": v(5.79, -45.97) * mm});
            skLineSegment(sketch, "E11.0.6.50", {"start": v(-33.53, -68.3) * mm, "end": v(-22.4, -68.3) * mm});
            skLineSegment(sketch, "E11.0.6.51", {"start": v(22.86, -68.3) * mm, "end": v(33.98, -68.3) * mm});
            skPoint(sketch, "E11.0.6.52", {"position": v(17.78, -45.97) * mm});
            skLineSegment(sketch, "E11.0.6.53", {"start": v(79.25, -68.3) * mm, "end": v(90.37, -68.3) * mm});
            skLineSegment(sketch, "E11.0.6.54", {"start": v(135.64, -68.3) * mm, "end": v(146.76, -68.3) * mm});
            skPoint(sketch, "E11.0.6.55", {"position": v(67.26, -68.3) * mm});
            skPoint(sketch, "E11.0.6.56", {"position": v(-101.9, -45.97) * mm});
            skPoint(sketch, "E11.0.6.57", {"position": v(10.87, -68.3) * mm});
            skPoint(sketch, "E11.0.6.58", {"position": v(123.65, -68.3) * mm});
            skPoint(sketch, "E11.0.6.59", {"position": v(-45.52, -68.3) * mm});
            skPoint(sketch, "E11.0.6.60", {"position": v(-95, -68.3) * mm});
            skLineSegment(sketch, "E11.0.6.61", {"start": v(51.05, -68.3) * mm, "end": v(62.18, -68.3) * mm});
            skPoint(sketch, "E11.0.6.62", {"position": v(17.78, -68.3) * mm});
            skLineSegment(sketch, "E11.0.6.63", {"start": v(107.44, -68.3) * mm, "end": v(118.57, -68.3) * mm});
            skLineSegment(sketch, "E11.0.6.64", {"start": v(-61.72, -68.3) * mm, "end": v(-50.6, -68.3) * mm});
            skLineSegment(sketch, "E11.0.6.65", {"start": v(-5.33, -68.3) * mm, "end": v(5.79, -68.3) * mm});
            skPoint(sketch, "E11.0.6.66", {"position": v(-123.2, -45.97) * mm});
            skPoint(sketch, "E11.0.6.67", {"position": v(-10.41, -45.97) * mm});
            skPoint(sketch, "E11.0.6.68", {"position": v(102.36, -45.97) * mm});
            skPoint(sketch, "E11.0.6.69", {"position": v(74.17, -45.97) * mm});
            skPoint(sketch, "E11.0.6.70", {"position": v(-10.41, -68.3) * mm});
            skPoint(sketch, "E11.0.6.71", {"position": v(102.36, -68.3) * mm});
            skPoint(sketch, "E11.0.6.72", {"position": v(-38.6, -45.97) * mm});
            skPoint(sketch, "E11.0.6.73", {"position": v(-123.2, -68.3) * mm});
            skPoint(sketch, "E11.0.6.74", {"position": v(-95, -45.97) * mm});
            skLineSegment(sketch, "E11.0.6.75", {"start": v(-38.6, -51.05) * mm, "end": v(-38.6, -63.23) * mm});
            skLineSegment(sketch, "E11.0.6.76", {"start": v(17.78, -51.05) * mm, "end": v(17.78, -63.23) * mm});
            skLineSegment(sketch, "E11.0.6.77", {"start": v(74.17, -51.05) * mm, "end": v(74.17, -63.23) * mm});
            skLineSegment(sketch, "E11.0.6.78", {"start": v(130.56, -51.05) * mm, "end": v(130.56, -63.23) * mm});
            skLineSegment(sketch, "E11.0.6.79", {"start": v(-118.11, -68.3) * mm, "end": v(-106.99, -68.3) * mm});
            skLineSegment(sketch, "E11.0.6.80", {"start": v(-89.92, -45.97) * mm, "end": v(-78.8, -45.97) * mm});
            skLineSegment(sketch, "E11.0.6.81", {"start": v(-78.8, -45.97) * mm, "end": v(-73.71, -51.05) * mm});
            skLineSegment(sketch, "E11.0.6.82", {"start": v(-95, -63.23) * mm, "end": v(-89.92, -68.3) * mm});
            skLineSegment(sketch, "E11.0.6.83", {"start": v(33.98, -45.97) * mm, "end": v(39.06, -51.05) * mm});
            skLineSegment(sketch, "E11.0.6.84", {"start": v(-73.71, -63.23) * mm, "end": v(-78.8, -68.3) * mm});
            skLineSegment(sketch, "E11.0.6.85", {"start": v(-123.2, -51.05) * mm, "end": v(-118.11, -45.97) * mm});
            skLineSegment(sketch, "E11.0.6.86", {"start": v(-106.99, -45.97) * mm, "end": v(-101.9, -51.05) * mm});
            skLineSegment(sketch, "E11.0.6.87", {"start": v(-123.2, -63.23) * mm, "end": v(-118.11, -68.3) * mm});
            skLineSegment(sketch, "E11.0.6.88", {"start": v(-101.9, -63.23) * mm, "end": v(-106.99, -68.3) * mm});
            skLineSegment(sketch, "E11.0.6.89", {"start": v(-45.52, -63.23) * mm, "end": v(-50.6, -68.3) * mm});
            skLineSegment(sketch, "E11.0.6.90", {"start": v(10.87, -63.23) * mm, "end": v(5.79, -68.3) * mm});
            skLineSegment(sketch, "E11.0.6.91", {"start": v(67.26, -63.23) * mm, "end": v(62.18, -68.3) * mm});
            skLineSegment(sketch, "E11.0.6.92", {"start": v(123.65, -63.23) * mm, "end": v(118.57, -68.3) * mm});
            skLineSegment(sketch, "E11.0.6.93", {"start": v(62.18, -45.97) * mm, "end": v(67.26, -51.05) * mm});
            skLineSegment(sketch, "E11.0.6.94", {"start": v(39.06, -63.23) * mm, "end": v(33.98, -68.3) * mm});
            skLineSegment(sketch, "E11.0.6.95", {"start": v(118.57, -45.97) * mm, "end": v(123.65, -51.05) * mm});
            skLineSegment(sketch, "E11.0.6.96", {"start": v(95.45, -63.23) * mm, "end": v(90.37, -68.3) * mm});
            skLineSegment(sketch, "E11.0.6.97", {"start": v(151.84, -63.23) * mm, "end": v(146.76, -68.3) * mm});
            skLineSegment(sketch, "E11.0.6.98", {"start": v(-50.6, -45.97) * mm, "end": v(-45.52, -51.05) * mm});
            skLineSegment(sketch, "E11.0.6.99", {"start": v(5.79, -45.97) * mm, "end": v(10.87, -51.05) * mm});
            skLineSegment(sketch, "E11.0.6.100", {"start": v(-17.32, -63.23) * mm, "end": v(-22.4, -68.3) * mm});
            skLineSegment(sketch, "E11.0.6.101", {"start": v(-38.6, -63.23) * mm, "end": v(-33.53, -68.3) * mm});
            skLineSegment(sketch, "E11.0.6.102", {"start": v(-10.41, -51.05) * mm, "end": v(-5.33, -45.97) * mm});
            skLineSegment(sketch, "E11.0.6.103", {"start": v(-66.8, -51.05) * mm, "end": v(-61.72, -45.97) * mm});
            skLineSegment(sketch, "E11.0.6.104", {"start": v(130.56, -63.23) * mm, "end": v(135.64, -68.3) * mm});
            skLineSegment(sketch, "E11.0.6.105", {"start": v(102.36, -51.05) * mm, "end": v(107.44, -45.97) * mm});
            skLineSegment(sketch, "E11.0.6.106", {"start": v(74.17, -63.23) * mm, "end": v(79.25, -68.3) * mm});
            skLineSegment(sketch, "E11.0.6.107", {"start": v(45.97, -51.05) * mm, "end": v(51.05, -45.97) * mm});
            skLineSegment(sketch, "E11.0.6.108", {"start": v(17.78, -63.23) * mm, "end": v(22.86, -68.3) * mm});
            skLineSegment(sketch, "E11.0.6.109", {"start": v(130.56, -51.05) * mm, "end": v(135.64, -45.97) * mm});
            skLineSegment(sketch, "E11.0.6.110", {"start": v(74.17, -51.05) * mm, "end": v(79.25, -45.97) * mm});
            skLineSegment(sketch, "E11.0.6.111", {"start": v(17.78, -51.05) * mm, "end": v(22.86, -45.97) * mm});
            skLineSegment(sketch, "E11.0.6.112", {"start": v(-95, -51.05) * mm, "end": v(-89.92, -45.97) * mm});
            skLineSegment(sketch, "E11.0.6.113", {"start": v(-38.6, -51.05) * mm, "end": v(-33.53, -45.97) * mm});
            skLineSegment(sketch, "E11.0.6.114", {"start": v(-22.4, -45.97) * mm, "end": v(-17.32, -51.05) * mm});
            skLineSegment(sketch, "E11.0.6.115", {"start": v(-10.41, -63.23) * mm, "end": v(-5.33, -68.3) * mm});
            skLineSegment(sketch, "E11.0.6.116", {"start": v(-66.8, -63.23) * mm, "end": v(-61.72, -68.3) * mm});
            skLineSegment(sketch, "E11.0.6.117", {"start": v(146.76, -45.97) * mm, "end": v(151.84, -51.05) * mm});
            skLineSegment(sketch, "E11.0.6.118", {"start": v(102.36, -63.23) * mm, "end": v(107.44, -68.3) * mm});
            skLineSegment(sketch, "E11.0.6.119", {"start": v(90.37, -45.97) * mm, "end": v(95.45, -51.05) * mm});
            skLineSegment(sketch, "E11.0.6.120", {"start": v(45.97, -63.23) * mm, "end": v(51.05, -68.3) * mm});
            skPoint(sketch, "E11.0.7.0", {"position": v(-73.71, -74.17) * mm});
            skLineSegment(sketch, "E11.0.7.1", {"start": v(102.36, -79.25) * mm, "end": v(102.36, -91.42) * mm});
            skLineSegment(sketch, "E11.0.7.2", {"start": v(45.97, -79.25) * mm, "end": v(45.97, -91.42) * mm});
            skPoint(sketch, "E11.0.7.3", {"position": v(39.06, -74.17) * mm});
            skLineSegment(sketch, "E11.0.7.4", {"start": v(-66.8, -79.25) * mm, "end": v(-66.8, -91.42) * mm});
            skLineSegment(sketch, "E11.0.7.5", {"start": v(-95, -79.25) * mm, "end": v(-95, -91.42) * mm});
            skLineSegment(sketch, "E11.0.7.6", {"start": v(-73.71, -79.25) * mm, "end": v(-73.71, -91.42) * mm});
            skLineSegment(sketch, "E11.0.7.7", {"start": v(-123.2, -79.25) * mm, "end": v(-123.2, -91.42) * mm});
            skLineSegment(sketch, "E11.0.7.8", {"start": v(-101.9, -79.25) * mm, "end": v(-101.9, -91.42) * mm});
            skPoint(sketch, "E11.0.7.9", {"position": v(130.56, -96.5) * mm});
            skPoint(sketch, "E11.0.7.10", {"position": v(67.26, -74.17) * mm});
            skPoint(sketch, "E11.0.7.11", {"position": v(-66.8, -96.5) * mm});
            skPoint(sketch, "E11.0.7.12", {"position": v(10.87, -74.17) * mm});
            skPoint(sketch, "E11.0.7.13", {"position": v(-101.9, -96.5) * mm});
            skPoint(sketch, "E11.0.7.14", {"position": v(45.97, -96.5) * mm});
            skLineSegment(sketch, "E11.0.7.15", {"start": v(-118.11, -74.17) * mm, "end": v(-106.99, -74.17) * mm});
            skPoint(sketch, "E11.0.7.16", {"position": v(-45.52, -74.17) * mm});
            skPoint(sketch, "E11.0.7.17", {"position": v(151.84, -74.17) * mm});
            skPoint(sketch, "E11.0.7.18", {"position": v(123.65, -74.17) * mm});
            skLineSegment(sketch, "E11.0.7.19", {"start": v(151.84, -79.25) * mm, "end": v(151.84, -91.42) * mm});
            skLineSegment(sketch, "E11.0.7.20", {"start": v(95.45, -79.25) * mm, "end": v(95.45, -91.42) * mm});
            skLineSegment(sketch, "E11.0.7.21", {"start": v(39.06, -79.25) * mm, "end": v(39.06, -91.42) * mm});
            skLineSegment(sketch, "E11.0.7.22", {"start": v(-17.32, -79.25) * mm, "end": v(-17.32, -91.42) * mm});
            skPoint(sketch, "E11.0.7.23", {"position": v(74.17, -96.5) * mm});
            skPoint(sketch, "E11.0.7.24", {"position": v(-38.6, -96.5) * mm});
            skLineSegment(sketch, "E11.0.7.25", {"start": v(-10.41, -79.25) * mm, "end": v(-10.41, -91.42) * mm});
            skLineSegment(sketch, "E11.0.7.26", {"start": v(-89.92, -96.5) * mm, "end": v(-78.8, -96.5) * mm});
            skLineSegment(sketch, "E11.0.7.27", {"start": v(-45.52, -79.25) * mm, "end": v(-45.52, -91.42) * mm});
            skLineSegment(sketch, "E11.0.7.28", {"start": v(10.87, -79.25) * mm, "end": v(10.87, -91.42) * mm});
            skPoint(sketch, "E11.0.7.29", {"position": v(-17.32, -74.17) * mm});
            skPoint(sketch, "E11.0.7.30", {"position": v(95.45, -74.17) * mm});
            skPoint(sketch, "E11.0.7.31", {"position": v(95.45, -96.5) * mm});
            skPoint(sketch, "E11.0.7.32", {"position": v(151.84, -96.5) * mm});
            skPoint(sketch, "E11.0.7.33", {"position": v(-73.71, -96.5) * mm});
            skPoint(sketch, "E11.0.7.34", {"position": v(39.06, -96.5) * mm});
            skLineSegment(sketch, "E11.0.7.35", {"start": v(67.26, -79.25) * mm, "end": v(67.26, -91.42) * mm});
            skLineSegment(sketch, "E11.0.7.36", {"start": v(123.65, -79.25) * mm, "end": v(123.65, -91.42) * mm});
            skLineSegment(sketch, "E11.0.7.37", {"start": v(-123.2, -96.5) * mm, "end": v(-95, -96.5) * mm, "construction": true});
            skPoint(sketch, "E11.0.7.38", {"position": v(130.56, -74.17) * mm});
            skPoint(sketch, "E11.0.7.39", {"position": v(45.97, -74.17) * mm});
            skLineSegment(sketch, "E11.0.7.40", {"start": v(51.05, -74.17) * mm, "end": v(62.18, -74.17) * mm});
            skPoint(sketch, "E11.0.7.41", {"position": v(-66.8, -74.17) * mm});
            skLineSegment(sketch, "E11.0.7.42", {"start": v(107.44, -74.17) * mm, "end": v(118.57, -74.17) * mm});
            skLineSegment(sketch, "E11.0.7.43", {"start": v(135.64, -74.17) * mm, "end": v(146.76, -74.17) * mm});
            skLineSegment(sketch, "E11.0.7.44", {"start": v(79.25, -74.17) * mm, "end": v(90.37, -74.17) * mm});
            skLineSegment(sketch, "E11.0.7.45", {"start": v(22.86, -74.17) * mm, "end": v(33.98, -74.17) * mm});
            skLineSegment(sketch, "E11.0.7.46", {"start": v(-33.53, -74.17) * mm, "end": v(-22.4, -74.17) * mm});
            skLineSegment(sketch, "E11.0.7.47", {"start": v(-61.72, -74.17) * mm, "end": v(-50.6, -74.17) * mm});
            skPoint(sketch, "E11.0.7.48", {"position": v(-17.32, -96.5) * mm});
            skLineSegment(sketch, "E11.0.7.49", {"start": v(-5.33, -74.17) * mm, "end": v(5.79, -74.17) * mm});
            skLineSegment(sketch, "E11.0.7.50", {"start": v(-33.53, -96.5) * mm, "end": v(-22.4, -96.5) * mm});
            skLineSegment(sketch, "E11.0.7.51", {"start": v(22.86, -96.5) * mm, "end": v(33.98, -96.5) * mm});
            skPoint(sketch, "E11.0.7.52", {"position": v(17.78, -74.17) * mm});
            skLineSegment(sketch, "E11.0.7.53", {"start": v(79.25, -96.5) * mm, "end": v(90.37, -96.5) * mm});
            skLineSegment(sketch, "E11.0.7.54", {"start": v(135.64, -96.5) * mm, "end": v(146.76, -96.5) * mm});
            skPoint(sketch, "E11.0.7.55", {"position": v(67.26, -96.5) * mm});
            skPoint(sketch, "E11.0.7.56", {"position": v(-101.9, -74.17) * mm});
            skPoint(sketch, "E11.0.7.57", {"position": v(10.87, -96.5) * mm});
            skPoint(sketch, "E11.0.7.58", {"position": v(123.65, -96.5) * mm});
            skPoint(sketch, "E11.0.7.59", {"position": v(-45.52, -96.5) * mm});
            skPoint(sketch, "E11.0.7.60", {"position": v(-95, -96.5) * mm});
            skLineSegment(sketch, "E11.0.7.61", {"start": v(51.05, -96.5) * mm, "end": v(62.18, -96.5) * mm});
            skPoint(sketch, "E11.0.7.62", {"position": v(17.78, -96.5) * mm});
            skLineSegment(sketch, "E11.0.7.63", {"start": v(107.44, -96.5) * mm, "end": v(118.57, -96.5) * mm});
            skLineSegment(sketch, "E11.0.7.64", {"start": v(-61.72, -96.5) * mm, "end": v(-50.6, -96.5) * mm});
            skLineSegment(sketch, "E11.0.7.65", {"start": v(-5.33, -96.5) * mm, "end": v(5.79, -96.5) * mm});
            skPoint(sketch, "E11.0.7.66", {"position": v(-123.2, -74.17) * mm});
            skPoint(sketch, "E11.0.7.67", {"position": v(-10.41, -74.17) * mm});
            skPoint(sketch, "E11.0.7.68", {"position": v(102.36, -74.17) * mm});
            skPoint(sketch, "E11.0.7.69", {"position": v(74.17, -74.17) * mm});
            skPoint(sketch, "E11.0.7.70", {"position": v(-10.41, -96.5) * mm});
            skPoint(sketch, "E11.0.7.71", {"position": v(102.36, -96.5) * mm});
            skPoint(sketch, "E11.0.7.72", {"position": v(-38.6, -74.17) * mm});
            skPoint(sketch, "E11.0.7.73", {"position": v(-123.2, -96.5) * mm});
            skPoint(sketch, "E11.0.7.74", {"position": v(-95, -74.17) * mm});
            skLineSegment(sketch, "E11.0.7.75", {"start": v(-38.6, -79.25) * mm, "end": v(-38.6, -91.42) * mm});
            skLineSegment(sketch, "E11.0.7.76", {"start": v(17.78, -79.25) * mm, "end": v(17.78, -91.42) * mm});
            skLineSegment(sketch, "E11.0.7.77", {"start": v(74.17, -79.25) * mm, "end": v(74.17, -91.42) * mm});
            skLineSegment(sketch, "E11.0.7.78", {"start": v(130.56, -79.25) * mm, "end": v(130.56, -91.42) * mm});
            skLineSegment(sketch, "E11.0.7.79", {"start": v(-118.11, -96.5) * mm, "end": v(-106.99, -96.5) * mm});
            skLineSegment(sketch, "E11.0.7.80", {"start": v(-89.92, -74.17) * mm, "end": v(-78.8, -74.17) * mm});
            skLineSegment(sketch, "E11.0.7.81", {"start": v(-78.8, -74.17) * mm, "end": v(-73.71, -79.25) * mm});
            skLineSegment(sketch, "E11.0.7.82", {"start": v(-95, -91.42) * mm, "end": v(-89.92, -96.5) * mm});
            skLineSegment(sketch, "E11.0.7.83", {"start": v(33.98, -74.17) * mm, "end": v(39.06, -79.25) * mm});
            skLineSegment(sketch, "E11.0.7.84", {"start": v(-73.71, -91.42) * mm, "end": v(-78.8, -96.5) * mm});
            skLineSegment(sketch, "E11.0.7.85", {"start": v(-123.2, -79.25) * mm, "end": v(-118.11, -74.17) * mm});
            skLineSegment(sketch, "E11.0.7.86", {"start": v(-106.99, -74.17) * mm, "end": v(-101.9, -79.25) * mm});
            skLineSegment(sketch, "E11.0.7.87", {"start": v(-123.2, -91.42) * mm, "end": v(-118.11, -96.5) * mm});
            skLineSegment(sketch, "E11.0.7.88", {"start": v(-101.9, -91.42) * mm, "end": v(-106.99, -96.5) * mm});
            skLineSegment(sketch, "E11.0.7.89", {"start": v(-45.52, -91.42) * mm, "end": v(-50.6, -96.5) * mm});
            skLineSegment(sketch, "E11.0.7.90", {"start": v(10.87, -91.42) * mm, "end": v(5.79, -96.5) * mm});
            skLineSegment(sketch, "E11.0.7.91", {"start": v(67.26, -91.42) * mm, "end": v(62.18, -96.5) * mm});
            skLineSegment(sketch, "E11.0.7.92", {"start": v(123.65, -91.42) * mm, "end": v(118.57, -96.5) * mm});
            skLineSegment(sketch, "E11.0.7.93", {"start": v(62.18, -74.17) * mm, "end": v(67.26, -79.25) * mm});
            skLineSegment(sketch, "E11.0.7.94", {"start": v(39.06, -91.42) * mm, "end": v(33.98, -96.5) * mm});
            skLineSegment(sketch, "E11.0.7.95", {"start": v(118.57, -74.17) * mm, "end": v(123.65, -79.25) * mm});
            skLineSegment(sketch, "E11.0.7.96", {"start": v(95.45, -91.42) * mm, "end": v(90.37, -96.5) * mm});
            skLineSegment(sketch, "E11.0.7.97", {"start": v(151.84, -91.42) * mm, "end": v(146.76, -96.5) * mm});
            skLineSegment(sketch, "E11.0.7.98", {"start": v(-50.6, -74.17) * mm, "end": v(-45.52, -79.25) * mm});
            skLineSegment(sketch, "E11.0.7.99", {"start": v(5.79, -74.17) * mm, "end": v(10.87, -79.25) * mm});
            skLineSegment(sketch, "E11.0.7.100", {"start": v(-17.32, -91.42) * mm, "end": v(-22.4, -96.5) * mm});
            skLineSegment(sketch, "E11.0.7.101", {"start": v(-38.6, -91.42) * mm, "end": v(-33.53, -96.5) * mm});
            skLineSegment(sketch, "E11.0.7.102", {"start": v(-10.41, -79.25) * mm, "end": v(-5.33, -74.17) * mm});
            skLineSegment(sketch, "E11.0.7.103", {"start": v(-66.8, -79.25) * mm, "end": v(-61.72, -74.17) * mm});
            skLineSegment(sketch, "E11.0.7.104", {"start": v(130.56, -91.42) * mm, "end": v(135.64, -96.5) * mm});
            skLineSegment(sketch, "E11.0.7.105", {"start": v(102.36, -79.25) * mm, "end": v(107.44, -74.17) * mm});
            skLineSegment(sketch, "E11.0.7.106", {"start": v(74.17, -91.42) * mm, "end": v(79.25, -96.5) * mm});
            skLineSegment(sketch, "E11.0.7.107", {"start": v(45.97, -79.25) * mm, "end": v(51.05, -74.17) * mm});
            skLineSegment(sketch, "E11.0.7.108", {"start": v(17.78, -91.42) * mm, "end": v(22.86, -96.5) * mm});
            skLineSegment(sketch, "E11.0.7.109", {"start": v(130.56, -79.25) * mm, "end": v(135.64, -74.17) * mm});
            skLineSegment(sketch, "E11.0.7.110", {"start": v(74.17, -79.25) * mm, "end": v(79.25, -74.17) * mm});
            skLineSegment(sketch, "E11.0.7.111", {"start": v(17.78, -79.25) * mm, "end": v(22.86, -74.17) * mm});
            skLineSegment(sketch, "E11.0.7.112", {"start": v(-95, -79.25) * mm, "end": v(-89.92, -74.17) * mm});
            skLineSegment(sketch, "E11.0.7.113", {"start": v(-38.6, -79.25) * mm, "end": v(-33.53, -74.17) * mm});
            skLineSegment(sketch, "E11.0.7.114", {"start": v(-22.4, -74.17) * mm, "end": v(-17.32, -79.25) * mm});
            skLineSegment(sketch, "E11.0.7.115", {"start": v(-10.41, -91.42) * mm, "end": v(-5.33, -96.5) * mm});
            skLineSegment(sketch, "E11.0.7.116", {"start": v(-66.8, -91.42) * mm, "end": v(-61.72, -96.5) * mm});
            skLineSegment(sketch, "E11.0.7.117", {"start": v(146.76, -74.17) * mm, "end": v(151.84, -79.25) * mm});
            skLineSegment(sketch, "E11.0.7.118", {"start": v(102.36, -91.42) * mm, "end": v(107.44, -96.5) * mm});
            skLineSegment(sketch, "E11.0.7.119", {"start": v(90.37, -74.17) * mm, "end": v(95.45, -79.25) * mm});
            skLineSegment(sketch, "E11.0.7.120", {"start": v(45.97, -91.42) * mm, "end": v(51.05, -96.5) * mm});
            skPoint(sketch, "E11.0.8.0", {"position": v(-73.71, -102.36) * mm});
            skLineSegment(sketch, "E11.0.8.1", {"start": v(102.36, -107.44) * mm, "end": v(102.36, -119.62) * mm});
            skLineSegment(sketch, "E11.0.8.2", {"start": v(45.97, -107.44) * mm, "end": v(45.97, -119.62) * mm});
            skPoint(sketch, "E11.0.8.3", {"position": v(39.06, -102.36) * mm});
            skLineSegment(sketch, "E11.0.8.4", {"start": v(-66.8, -107.44) * mm, "end": v(-66.8, -119.62) * mm});
            skLineSegment(sketch, "E11.0.8.5", {"start": v(-95, -107.44) * mm, "end": v(-95, -119.62) * mm});
            skLineSegment(sketch, "E11.0.8.6", {"start": v(-73.71, -107.44) * mm, "end": v(-73.71, -119.62) * mm});
            skLineSegment(sketch, "E11.0.8.7", {"start": v(-123.2, -107.44) * mm, "end": v(-123.2, -119.62) * mm});
            skLineSegment(sketch, "E11.0.8.8", {"start": v(-101.9, -107.44) * mm, "end": v(-101.9, -119.62) * mm});
            skPoint(sketch, "E11.0.8.9", {"position": v(130.56, -124.7) * mm});
            skPoint(sketch, "E11.0.8.10", {"position": v(67.26, -102.36) * mm});
            skPoint(sketch, "E11.0.8.11", {"position": v(-66.8, -124.7) * mm});
            skPoint(sketch, "E11.0.8.12", {"position": v(10.87, -102.36) * mm});
            skPoint(sketch, "E11.0.8.13", {"position": v(-101.9, -124.7) * mm});
            skPoint(sketch, "E11.0.8.14", {"position": v(45.97, -124.7) * mm});
            skLineSegment(sketch, "E11.0.8.15", {"start": v(-118.11, -102.36) * mm, "end": v(-106.99, -102.36) * mm});
            skPoint(sketch, "E11.0.8.16", {"position": v(-45.52, -102.36) * mm});
            skPoint(sketch, "E11.0.8.17", {"position": v(151.84, -102.36) * mm});
            skPoint(sketch, "E11.0.8.18", {"position": v(123.65, -102.36) * mm});
            skLineSegment(sketch, "E11.0.8.19", {"start": v(151.84, -107.44) * mm, "end": v(151.84, -119.62) * mm});
            skLineSegment(sketch, "E11.0.8.20", {"start": v(95.45, -107.44) * mm, "end": v(95.45, -119.62) * mm});
            skLineSegment(sketch, "E11.0.8.21", {"start": v(39.06, -107.44) * mm, "end": v(39.06, -119.62) * mm});
            skLineSegment(sketch, "E11.0.8.22", {"start": v(-17.32, -107.44) * mm, "end": v(-17.32, -119.62) * mm});
            skPoint(sketch, "E11.0.8.23", {"position": v(74.17, -124.7) * mm});
            skPoint(sketch, "E11.0.8.24", {"position": v(-38.6, -124.7) * mm});
            skLineSegment(sketch, "E11.0.8.25", {"start": v(-10.41, -107.44) * mm, "end": v(-10.41, -119.62) * mm});
            skLineSegment(sketch, "E11.0.8.26", {"start": v(-89.92, -124.7) * mm, "end": v(-78.8, -124.7) * mm});
            skLineSegment(sketch, "E11.0.8.27", {"start": v(-45.52, -107.44) * mm, "end": v(-45.52, -119.62) * mm});
            skLineSegment(sketch, "E11.0.8.28", {"start": v(10.87, -107.44) * mm, "end": v(10.87, -119.62) * mm});
            skPoint(sketch, "E11.0.8.29", {"position": v(-17.32, -102.36) * mm});
            skPoint(sketch, "E11.0.8.30", {"position": v(95.45, -102.36) * mm});
            skPoint(sketch, "E11.0.8.31", {"position": v(95.45, -124.7) * mm});
            skPoint(sketch, "E11.0.8.32", {"position": v(151.84, -124.7) * mm});
            skPoint(sketch, "E11.0.8.33", {"position": v(-73.71, -124.7) * mm});
            skPoint(sketch, "E11.0.8.34", {"position": v(39.06, -124.7) * mm});
            skLineSegment(sketch, "E11.0.8.35", {"start": v(67.26, -107.44) * mm, "end": v(67.26, -119.62) * mm});
            skLineSegment(sketch, "E11.0.8.36", {"start": v(123.65, -107.44) * mm, "end": v(123.65, -119.62) * mm});
            skLineSegment(sketch, "E11.0.8.37", {"start": v(-123.2, -124.7) * mm, "end": v(-95, -124.7) * mm, "construction": true});
            skPoint(sketch, "E11.0.8.38", {"position": v(130.56, -102.36) * mm});
            skPoint(sketch, "E11.0.8.39", {"position": v(45.97, -102.36) * mm});
            skLineSegment(sketch, "E11.0.8.40", {"start": v(51.05, -102.36) * mm, "end": v(62.18, -102.36) * mm});
            skPoint(sketch, "E11.0.8.41", {"position": v(-66.8, -102.36) * mm});
            skLineSegment(sketch, "E11.0.8.42", {"start": v(107.44, -102.36) * mm, "end": v(118.57, -102.36) * mm});
            skLineSegment(sketch, "E11.0.8.43", {"start": v(135.64, -102.36) * mm, "end": v(146.76, -102.36) * mm});
            skLineSegment(sketch, "E11.0.8.44", {"start": v(79.25, -102.36) * mm, "end": v(90.37, -102.36) * mm});
            skLineSegment(sketch, "E11.0.8.45", {"start": v(22.86, -102.36) * mm, "end": v(33.98, -102.36) * mm});
            skLineSegment(sketch, "E11.0.8.46", {"start": v(-33.53, -102.36) * mm, "end": v(-22.4, -102.36) * mm});
            skLineSegment(sketch, "E11.0.8.47", {"start": v(-61.72, -102.36) * mm, "end": v(-50.6, -102.36) * mm});
            skPoint(sketch, "E11.0.8.48", {"position": v(-17.32, -124.7) * mm});
            skLineSegment(sketch, "E11.0.8.49", {"start": v(-5.33, -102.36) * mm, "end": v(5.79, -102.36) * mm});
            skLineSegment(sketch, "E11.0.8.50", {"start": v(-33.53, -124.7) * mm, "end": v(-22.4, -124.7) * mm});
            skLineSegment(sketch, "E11.0.8.51", {"start": v(22.86, -124.7) * mm, "end": v(33.98, -124.7) * mm});
            skPoint(sketch, "E11.0.8.52", {"position": v(17.78, -102.36) * mm});
            skLineSegment(sketch, "E11.0.8.53", {"start": v(79.25, -124.7) * mm, "end": v(90.37, -124.7) * mm});
            skLineSegment(sketch, "E11.0.8.54", {"start": v(135.64, -124.7) * mm, "end": v(146.76, -124.7) * mm});
            skPoint(sketch, "E11.0.8.55", {"position": v(67.26, -124.7) * mm});
            skPoint(sketch, "E11.0.8.56", {"position": v(-101.9, -102.36) * mm});
            skPoint(sketch, "E11.0.8.57", {"position": v(10.87, -124.7) * mm});
            skPoint(sketch, "E11.0.8.58", {"position": v(123.65, -124.7) * mm});
            skPoint(sketch, "E11.0.8.59", {"position": v(-45.52, -124.7) * mm});
            skPoint(sketch, "E11.0.8.60", {"position": v(-95, -124.7) * mm});
            skLineSegment(sketch, "E11.0.8.61", {"start": v(51.05, -124.7) * mm, "end": v(62.18, -124.7) * mm});
            skPoint(sketch, "E11.0.8.62", {"position": v(17.78, -124.7) * mm});
            skLineSegment(sketch, "E11.0.8.63", {"start": v(107.44, -124.7) * mm, "end": v(118.57, -124.7) * mm});
            skLineSegment(sketch, "E11.0.8.64", {"start": v(-61.72, -124.7) * mm, "end": v(-50.6, -124.7) * mm});
            skLineSegment(sketch, "E11.0.8.65", {"start": v(-5.33, -124.7) * mm, "end": v(5.79, -124.7) * mm});
            skPoint(sketch, "E11.0.8.66", {"position": v(-123.2, -102.36) * mm});
            skPoint(sketch, "E11.0.8.67", {"position": v(-10.41, -102.36) * mm});
            skPoint(sketch, "E11.0.8.68", {"position": v(102.36, -102.36) * mm});
            skPoint(sketch, "E11.0.8.69", {"position": v(74.17, -102.36) * mm});
            skPoint(sketch, "E11.0.8.70", {"position": v(-10.41, -124.7) * mm});
            skPoint(sketch, "E11.0.8.71", {"position": v(102.36, -124.7) * mm});
            skPoint(sketch, "E11.0.8.72", {"position": v(-38.6, -102.36) * mm});
            skPoint(sketch, "E11.0.8.73", {"position": v(-123.2, -124.7) * mm});
            skPoint(sketch, "E11.0.8.74", {"position": v(-95, -102.36) * mm});
            skLineSegment(sketch, "E11.0.8.75", {"start": v(-38.6, -107.44) * mm, "end": v(-38.6, -119.62) * mm});
            skLineSegment(sketch, "E11.0.8.76", {"start": v(17.78, -107.44) * mm, "end": v(17.78, -119.62) * mm});
            skLineSegment(sketch, "E11.0.8.77", {"start": v(74.17, -107.44) * mm, "end": v(74.17, -119.62) * mm});
            skLineSegment(sketch, "E11.0.8.78", {"start": v(130.56, -107.44) * mm, "end": v(130.56, -119.62) * mm});
            skLineSegment(sketch, "E11.0.8.79", {"start": v(-118.11, -124.7) * mm, "end": v(-106.99, -124.7) * mm});
            skLineSegment(sketch, "E11.0.8.80", {"start": v(-89.92, -102.36) * mm, "end": v(-78.8, -102.36) * mm});
            skLineSegment(sketch, "E11.0.8.81", {"start": v(-78.8, -102.36) * mm, "end": v(-73.71, -107.44) * mm});
            skLineSegment(sketch, "E11.0.8.82", {"start": v(-95, -119.62) * mm, "end": v(-89.92, -124.7) * mm});
            skLineSegment(sketch, "E11.0.8.83", {"start": v(33.98, -102.36) * mm, "end": v(39.06, -107.44) * mm});
            skLineSegment(sketch, "E11.0.8.84", {"start": v(-73.71, -119.62) * mm, "end": v(-78.8, -124.7) * mm});
            skLineSegment(sketch, "E11.0.8.85", {"start": v(-123.2, -107.44) * mm, "end": v(-118.11, -102.36) * mm});
            skLineSegment(sketch, "E11.0.8.86", {"start": v(-106.99, -102.36) * mm, "end": v(-101.9, -107.44) * mm});
            skLineSegment(sketch, "E11.0.8.87", {"start": v(-123.2, -119.62) * mm, "end": v(-118.11, -124.7) * mm});
            skLineSegment(sketch, "E11.0.8.88", {"start": v(-101.9, -119.62) * mm, "end": v(-106.99, -124.7) * mm});
            skLineSegment(sketch, "E11.0.8.89", {"start": v(-45.52, -119.62) * mm, "end": v(-50.6, -124.7) * mm});
            skLineSegment(sketch, "E11.0.8.90", {"start": v(10.87, -119.62) * mm, "end": v(5.79, -124.7) * mm});
            skLineSegment(sketch, "E11.0.8.91", {"start": v(67.26, -119.62) * mm, "end": v(62.18, -124.7) * mm});
            skLineSegment(sketch, "E11.0.8.92", {"start": v(123.65, -119.62) * mm, "end": v(118.57, -124.7) * mm});
            skLineSegment(sketch, "E11.0.8.93", {"start": v(62.18, -102.36) * mm, "end": v(67.26, -107.44) * mm});
            skLineSegment(sketch, "E11.0.8.94", {"start": v(39.06, -119.62) * mm, "end": v(33.98, -124.7) * mm});
            skLineSegment(sketch, "E11.0.8.95", {"start": v(118.57, -102.36) * mm, "end": v(123.65, -107.44) * mm});
            skLineSegment(sketch, "E11.0.8.96", {"start": v(95.45, -119.62) * mm, "end": v(90.37, -124.7) * mm});
            skLineSegment(sketch, "E11.0.8.97", {"start": v(151.84, -119.62) * mm, "end": v(146.76, -124.7) * mm});
            skLineSegment(sketch, "E11.0.8.98", {"start": v(-50.6, -102.36) * mm, "end": v(-45.52, -107.44) * mm});
            skLineSegment(sketch, "E11.0.8.99", {"start": v(5.79, -102.36) * mm, "end": v(10.87, -107.44) * mm});
            skLineSegment(sketch, "E11.0.8.100", {"start": v(-17.32, -119.62) * mm, "end": v(-22.4, -124.7) * mm});
            skLineSegment(sketch, "E11.0.8.101", {"start": v(-38.6, -119.62) * mm, "end": v(-33.53, -124.7) * mm});
            skLineSegment(sketch, "E11.0.8.102", {"start": v(-10.41, -107.44) * mm, "end": v(-5.33, -102.36) * mm});
            skLineSegment(sketch, "E11.0.8.103", {"start": v(-66.8, -107.44) * mm, "end": v(-61.72, -102.36) * mm});
            skLineSegment(sketch, "E11.0.8.104", {"start": v(130.56, -119.62) * mm, "end": v(135.64, -124.7) * mm});
            skLineSegment(sketch, "E11.0.8.105", {"start": v(102.36, -107.44) * mm, "end": v(107.44, -102.36) * mm});
            skLineSegment(sketch, "E11.0.8.106", {"start": v(74.17, -119.62) * mm, "end": v(79.25, -124.7) * mm});
            skLineSegment(sketch, "E11.0.8.107", {"start": v(45.97, -107.44) * mm, "end": v(51.05, -102.36) * mm});
            skLineSegment(sketch, "E11.0.8.108", {"start": v(17.78, -119.62) * mm, "end": v(22.86, -124.7) * mm});
            skLineSegment(sketch, "E11.0.8.109", {"start": v(130.56, -107.44) * mm, "end": v(135.64, -102.36) * mm});
            skLineSegment(sketch, "E11.0.8.110", {"start": v(74.17, -107.44) * mm, "end": v(79.25, -102.36) * mm});
            skLineSegment(sketch, "E11.0.8.111", {"start": v(17.78, -107.44) * mm, "end": v(22.86, -102.36) * mm});
            skLineSegment(sketch, "E11.0.8.112", {"start": v(-95, -107.44) * mm, "end": v(-89.92, -102.36) * mm});
            skLineSegment(sketch, "E11.0.8.113", {"start": v(-38.6, -107.44) * mm, "end": v(-33.53, -102.36) * mm});
            skLineSegment(sketch, "E11.0.8.114", {"start": v(-22.4, -102.36) * mm, "end": v(-17.32, -107.44) * mm});
            skLineSegment(sketch, "E11.0.8.115", {"start": v(-10.41, -119.62) * mm, "end": v(-5.33, -124.7) * mm});
            skLineSegment(sketch, "E11.0.8.116", {"start": v(-66.8, -119.62) * mm, "end": v(-61.72, -124.7) * mm});
            skLineSegment(sketch, "E11.0.8.117", {"start": v(146.76, -102.36) * mm, "end": v(151.84, -107.44) * mm});
            skLineSegment(sketch, "E11.0.8.118", {"start": v(102.36, -119.62) * mm, "end": v(107.44, -124.7) * mm});
            skLineSegment(sketch, "E11.0.8.119", {"start": v(90.37, -102.36) * mm, "end": v(95.45, -107.44) * mm});
            skLineSegment(sketch, "E11.0.8.120", {"start": v(45.97, -119.62) * mm, "end": v(51.05, -124.7) * mm});
            skPoint(sketch, "E11.0.9.0", {"position": v(-73.71, -130.56) * mm});
            skLineSegment(sketch, "E11.0.9.1", {"start": v(102.36, -135.64) * mm, "end": v(102.36, -147.81) * mm});
            skLineSegment(sketch, "E11.0.9.2", {"start": v(45.97, -135.64) * mm, "end": v(45.97, -147.81) * mm});
            skPoint(sketch, "E11.0.9.3", {"position": v(39.06, -130.56) * mm});
            skLineSegment(sketch, "E11.0.9.4", {"start": v(-66.8, -135.64) * mm, "end": v(-66.8, -147.81) * mm});
            skLineSegment(sketch, "E11.0.9.5", {"start": v(-95, -135.64) * mm, "end": v(-95, -147.81) * mm});
            skLineSegment(sketch, "E11.0.9.6", {"start": v(-73.71, -135.64) * mm, "end": v(-73.71, -147.81) * mm});
            skLineSegment(sketch, "E11.0.9.7", {"start": v(-123.2, -135.64) * mm, "end": v(-123.2, -147.81) * mm});
            skLineSegment(sketch, "E11.0.9.8", {"start": v(-101.9, -135.64) * mm, "end": v(-101.9, -147.81) * mm});
            skPoint(sketch, "E11.0.9.9", {"position": v(130.56, -152.9) * mm});
            skPoint(sketch, "E11.0.9.10", {"position": v(67.26, -130.56) * mm});
            skPoint(sketch, "E11.0.9.11", {"position": v(-66.8, -152.9) * mm});
            skPoint(sketch, "E11.0.9.12", {"position": v(10.87, -130.56) * mm});
            skPoint(sketch, "E11.0.9.13", {"position": v(-101.9, -152.9) * mm});
            skPoint(sketch, "E11.0.9.14", {"position": v(45.97, -152.9) * mm});
            skLineSegment(sketch, "E11.0.9.15", {"start": v(-118.11, -130.56) * mm, "end": v(-106.99, -130.56) * mm});
            skPoint(sketch, "E11.0.9.16", {"position": v(-45.52, -130.56) * mm});
            skPoint(sketch, "E11.0.9.17", {"position": v(151.84, -130.56) * mm});
            skPoint(sketch, "E11.0.9.18", {"position": v(123.65, -130.56) * mm});
            skLineSegment(sketch, "E11.0.9.19", {"start": v(151.84, -135.64) * mm, "end": v(151.84, -147.81) * mm});
            skLineSegment(sketch, "E11.0.9.20", {"start": v(95.45, -135.64) * mm, "end": v(95.45, -147.81) * mm});
            skLineSegment(sketch, "E11.0.9.21", {"start": v(39.06, -135.64) * mm, "end": v(39.06, -147.81) * mm});
            skLineSegment(sketch, "E11.0.9.22", {"start": v(-17.32, -135.64) * mm, "end": v(-17.32, -147.81) * mm});
            skPoint(sketch, "E11.0.9.23", {"position": v(74.17, -152.9) * mm});
            skPoint(sketch, "E11.0.9.24", {"position": v(-38.6, -152.9) * mm});
            skLineSegment(sketch, "E11.0.9.25", {"start": v(-10.41, -135.64) * mm, "end": v(-10.41, -147.81) * mm});
            skLineSegment(sketch, "E11.0.9.26", {"start": v(-89.92, -152.9) * mm, "end": v(-78.8, -152.9) * mm});
            skLineSegment(sketch, "E11.0.9.27", {"start": v(-45.52, -135.64) * mm, "end": v(-45.52, -147.81) * mm});
            skLineSegment(sketch, "E11.0.9.28", {"start": v(10.87, -135.64) * mm, "end": v(10.87, -147.81) * mm});
            skPoint(sketch, "E11.0.9.29", {"position": v(-17.32, -130.56) * mm});
            skPoint(sketch, "E11.0.9.30", {"position": v(95.45, -130.56) * mm});
            skPoint(sketch, "E11.0.9.31", {"position": v(95.45, -152.9) * mm});
            skPoint(sketch, "E11.0.9.32", {"position": v(151.84, -152.9) * mm});
            skPoint(sketch, "E11.0.9.33", {"position": v(-73.71, -152.9) * mm});
            skPoint(sketch, "E11.0.9.34", {"position": v(39.06, -152.9) * mm});
            skLineSegment(sketch, "E11.0.9.35", {"start": v(67.26, -135.64) * mm, "end": v(67.26, -147.81) * mm});
            skLineSegment(sketch, "E11.0.9.36", {"start": v(123.65, -135.64) * mm, "end": v(123.65, -147.81) * mm});
            skLineSegment(sketch, "E11.0.9.37", {"start": v(-123.2, -152.9) * mm, "end": v(-95, -152.9) * mm, "construction": true});
            skPoint(sketch, "E11.0.9.38", {"position": v(130.56, -130.56) * mm});
            skPoint(sketch, "E11.0.9.39", {"position": v(45.97, -130.56) * mm});
            skLineSegment(sketch, "E11.0.9.40", {"start": v(51.05, -130.56) * mm, "end": v(62.18, -130.56) * mm});
            skPoint(sketch, "E11.0.9.41", {"position": v(-66.8, -130.56) * mm});
            skLineSegment(sketch, "E11.0.9.42", {"start": v(107.44, -130.56) * mm, "end": v(118.57, -130.56) * mm});
            skLineSegment(sketch, "E11.0.9.43", {"start": v(135.64, -130.56) * mm, "end": v(146.76, -130.56) * mm});
            skLineSegment(sketch, "E11.0.9.44", {"start": v(79.25, -130.56) * mm, "end": v(90.37, -130.56) * mm});
            skLineSegment(sketch, "E11.0.9.45", {"start": v(22.86, -130.56) * mm, "end": v(33.98, -130.56) * mm});
            skLineSegment(sketch, "E11.0.9.46", {"start": v(-33.53, -130.56) * mm, "end": v(-22.4, -130.56) * mm});
            skLineSegment(sketch, "E11.0.9.47", {"start": v(-61.72, -130.56) * mm, "end": v(-50.6, -130.56) * mm});
            skPoint(sketch, "E11.0.9.48", {"position": v(-17.32, -152.9) * mm});
            skLineSegment(sketch, "E11.0.9.49", {"start": v(-5.33, -130.56) * mm, "end": v(5.79, -130.56) * mm});
            skLineSegment(sketch, "E11.0.9.50", {"start": v(-33.53, -152.9) * mm, "end": v(-22.4, -152.9) * mm});
            skLineSegment(sketch, "E11.0.9.51", {"start": v(22.86, -152.9) * mm, "end": v(33.98, -152.9) * mm});
            skPoint(sketch, "E11.0.9.52", {"position": v(17.78, -130.56) * mm});
            skLineSegment(sketch, "E11.0.9.53", {"start": v(79.25, -152.9) * mm, "end": v(90.37, -152.9) * mm});
            skLineSegment(sketch, "E11.0.9.54", {"start": v(135.64, -152.9) * mm, "end": v(146.76, -152.9) * mm});
            skPoint(sketch, "E11.0.9.55", {"position": v(67.26, -152.9) * mm});
            skPoint(sketch, "E11.0.9.56", {"position": v(-101.9, -130.56) * mm});
            skPoint(sketch, "E11.0.9.57", {"position": v(10.87, -152.9) * mm});
            skPoint(sketch, "E11.0.9.58", {"position": v(123.65, -152.9) * mm});
            skPoint(sketch, "E11.0.9.59", {"position": v(-45.52, -152.9) * mm});
            skPoint(sketch, "E11.0.9.60", {"position": v(-95, -152.9) * mm});
            skLineSegment(sketch, "E11.0.9.61", {"start": v(51.05, -152.9) * mm, "end": v(62.18, -152.9) * mm});
            skPoint(sketch, "E11.0.9.62", {"position": v(17.78, -152.9) * mm});
            skLineSegment(sketch, "E11.0.9.63", {"start": v(107.44, -152.9) * mm, "end": v(118.57, -152.9) * mm});
            skLineSegment(sketch, "E11.0.9.64", {"start": v(-61.72, -152.9) * mm, "end": v(-50.6, -152.9) * mm});
            skLineSegment(sketch, "E11.0.9.65", {"start": v(-5.33, -152.9) * mm, "end": v(5.79, -152.9) * mm});
            skPoint(sketch, "E11.0.9.66", {"position": v(-123.2, -130.56) * mm});
            skPoint(sketch, "E11.0.9.67", {"position": v(-10.41, -130.56) * mm});
            skPoint(sketch, "E11.0.9.68", {"position": v(102.36, -130.56) * mm});
            skPoint(sketch, "E11.0.9.69", {"position": v(74.17, -130.56) * mm});
            skPoint(sketch, "E11.0.9.70", {"position": v(-10.41, -152.9) * mm});
            skPoint(sketch, "E11.0.9.71", {"position": v(102.36, -152.9) * mm});
            skPoint(sketch, "E11.0.9.72", {"position": v(-38.6, -130.56) * mm});
            skPoint(sketch, "E11.0.9.73", {"position": v(-123.2, -152.9) * mm});
            skPoint(sketch, "E11.0.9.74", {"position": v(-95, -130.56) * mm});
            skLineSegment(sketch, "E11.0.9.75", {"start": v(-38.6, -135.64) * mm, "end": v(-38.6, -147.81) * mm});
            skLineSegment(sketch, "E11.0.9.76", {"start": v(17.78, -135.64) * mm, "end": v(17.78, -147.81) * mm});
            skLineSegment(sketch, "E11.0.9.77", {"start": v(74.17, -135.64) * mm, "end": v(74.17, -147.81) * mm});
            skLineSegment(sketch, "E11.0.9.78", {"start": v(130.56, -135.64) * mm, "end": v(130.56, -147.81) * mm});
            skLineSegment(sketch, "E11.0.9.79", {"start": v(-118.11, -152.9) * mm, "end": v(-106.99, -152.9) * mm});
            skLineSegment(sketch, "E11.0.9.80", {"start": v(-89.92, -130.56) * mm, "end": v(-78.8, -130.56) * mm});
            skLineSegment(sketch, "E11.0.9.81", {"start": v(-78.8, -130.56) * mm, "end": v(-73.71, -135.64) * mm});
            skLineSegment(sketch, "E11.0.9.82", {"start": v(-95, -147.81) * mm, "end": v(-89.92, -152.9) * mm});
            skLineSegment(sketch, "E11.0.9.83", {"start": v(33.98, -130.56) * mm, "end": v(39.06, -135.64) * mm});
            skLineSegment(sketch, "E11.0.9.84", {"start": v(-73.71, -147.81) * mm, "end": v(-78.8, -152.9) * mm});
            skLineSegment(sketch, "E11.0.9.85", {"start": v(-123.2, -135.64) * mm, "end": v(-118.11, -130.56) * mm});
            skLineSegment(sketch, "E11.0.9.86", {"start": v(-106.99, -130.56) * mm, "end": v(-101.9, -135.64) * mm});
            skLineSegment(sketch, "E11.0.9.87", {"start": v(-123.19, -147.81) * mm, "end": v(-118.11, -152.9) * mm});
            skLineSegment(sketch, "E11.0.9.88", {"start": v(-101.9, -147.81) * mm, "end": v(-106.99, -152.9) * mm});
            skLineSegment(sketch, "E11.0.9.89", {"start": v(-45.52, -147.81) * mm, "end": v(-50.6, -152.9) * mm});
            skLineSegment(sketch, "E11.0.9.90", {"start": v(10.87, -147.81) * mm, "end": v(5.79, -152.9) * mm});
            skLineSegment(sketch, "E11.0.9.91", {"start": v(67.26, -147.81) * mm, "end": v(62.18, -152.9) * mm});
            skLineSegment(sketch, "E11.0.9.92", {"start": v(123.65, -147.81) * mm, "end": v(118.57, -152.9) * mm});
            skLineSegment(sketch, "E11.0.9.93", {"start": v(62.18, -130.56) * mm, "end": v(67.26, -135.64) * mm});
            skLineSegment(sketch, "E11.0.9.94", {"start": v(39.06, -147.81) * mm, "end": v(33.98, -152.9) * mm});
            skLineSegment(sketch, "E11.0.9.95", {"start": v(118.57, -130.56) * mm, "end": v(123.65, -135.64) * mm});
            skLineSegment(sketch, "E11.0.9.96", {"start": v(95.45, -147.81) * mm, "end": v(90.37, -152.9) * mm});
            skLineSegment(sketch, "E11.0.9.97", {"start": v(151.84, -147.81) * mm, "end": v(146.76, -152.9) * mm});
            skLineSegment(sketch, "E11.0.9.98", {"start": v(-50.6, -130.56) * mm, "end": v(-45.52, -135.64) * mm});
            skLineSegment(sketch, "E11.0.9.99", {"start": v(5.79, -130.56) * mm, "end": v(10.87, -135.64) * mm});
            skLineSegment(sketch, "E11.0.9.100", {"start": v(-17.32, -147.81) * mm, "end": v(-22.4, -152.9) * mm});
            skLineSegment(sketch, "E11.0.9.101", {"start": v(-38.6, -147.81) * mm, "end": v(-33.53, -152.9) * mm});
            skLineSegment(sketch, "E11.0.9.102", {"start": v(-10.41, -135.64) * mm, "end": v(-5.33, -130.56) * mm});
            skLineSegment(sketch, "E11.0.9.103", {"start": v(-66.8, -135.64) * mm, "end": v(-61.72, -130.56) * mm});
            skLineSegment(sketch, "E11.0.9.104", {"start": v(130.56, -147.81) * mm, "end": v(135.64, -152.9) * mm});
            skLineSegment(sketch, "E11.0.9.105", {"start": v(102.36, -135.64) * mm, "end": v(107.44, -130.56) * mm});
            skLineSegment(sketch, "E11.0.9.106", {"start": v(74.17, -147.81) * mm, "end": v(79.25, -152.9) * mm});
            skLineSegment(sketch, "E11.0.9.107", {"start": v(45.97, -135.64) * mm, "end": v(51.05, -130.56) * mm});
            skLineSegment(sketch, "E11.0.9.108", {"start": v(17.78, -147.81) * mm, "end": v(22.86, -152.9) * mm});
            skLineSegment(sketch, "E11.0.9.109", {"start": v(130.56, -135.64) * mm, "end": v(135.64, -130.56) * mm});
            skLineSegment(sketch, "E11.0.9.110", {"start": v(74.17, -135.64) * mm, "end": v(79.25, -130.56) * mm});
            skLineSegment(sketch, "E11.0.9.111", {"start": v(17.78, -135.64) * mm, "end": v(22.86, -130.56) * mm});
            skLineSegment(sketch, "E11.0.9.112", {"start": v(-95, -135.64) * mm, "end": v(-89.92, -130.56) * mm});
            skLineSegment(sketch, "E11.0.9.113", {"start": v(-38.6, -135.64) * mm, "end": v(-33.53, -130.56) * mm});
            skLineSegment(sketch, "E11.0.9.114", {"start": v(-22.4, -130.56) * mm, "end": v(-17.32, -135.64) * mm});
            skLineSegment(sketch, "E11.0.9.115", {"start": v(-10.41, -147.81) * mm, "end": v(-5.33, -152.9) * mm});
            skLineSegment(sketch, "E11.0.9.116", {"start": v(-66.8, -147.81) * mm, "end": v(-61.72, -152.9) * mm});
            skLineSegment(sketch, "E11.0.9.117", {"start": v(146.76, -130.56) * mm, "end": v(151.84, -135.64) * mm});
            skLineSegment(sketch, "E11.0.9.118", {"start": v(102.36, -147.81) * mm, "end": v(107.44, -152.9) * mm});
            skLineSegment(sketch, "E11.0.9.119", {"start": v(90.37, -130.56) * mm, "end": v(95.45, -135.64) * mm});
            skLineSegment(sketch, "E11.0.9.120", {"start": v(45.97, -147.81) * mm, "end": v(51.05, -152.9) * mm});
            skLineSegment(sketch, "E11.direction1", {"start": v(-123.2, 100.85) * mm, "end": v(-97.8, 100.85) * mm, "construction": true});
            skLineSegment(sketch, "E11.direction2", {"start": v(-123.2, 100.85) * mm, "end": v(-123.2, 72.66) * mm, "construction": true});
            skSolve(sketch);
        }
        {
            var Q0;
            Q0=qSketchRegion(id+"F2",true);
            extrude(context, id + "F3", {"entities" : qUnion([Q0]), "operationType" : NewBodyOperationType.REMOVE, "oppositeDirection" : true, "depth" : 25.4 * mm, "offsetDistance" : 25.4 * mm});
        }
    });
